FREECAD ASSEMBLY — COMPONENT RECIPES ("enclosure-assy")

This assembly document has 8 components, labeled P0..P7 below (a component is one placed body or linked part). 8 of them carry a construction recipe — the FreeCAD feature program that regenerates the part from scratch, quoted from this document or its linked companion documents; the rest are supplied as boundary geometry only. No exploded tour is included for this assembly.
COMPONENT P0 — recipe-attached ("exhaust-fan", a linked part whose construction recipe lives in a companion FreeCAD document of the same project; that document's serialized recipe follows).
Construction recipe (the companion document, serialized — sketch geometry with constraints, then the solid features built on it; lengths are millimeters unless a unit is written):

FCSTD DOCUMENT  (FreeCAD 1.1R40971 (Git))
Label: exhaust-fan
License: All rights reserved
LicenseURL: http://en.wikipedia.org/wiki/All_rights_reserved
objects: Sketcher::SketchObject×3, PartDesign::Revolution×1, PartDesign::Pad×1, App::Point×1, Part::Feature×1, PartDesign::Body×1
note: 14 computed .brp shape members not serialized (recipe doc carries the construction recipe); baked Part::Feature solids carry a one-line shape summary decoded from their .brp

FEATURE [Sketcher::SketchObject] Sketch
  ArcFitTolerance = 0
  AttachmentSupport = -> [XZ_Plane]
  ExternalTypes = [0]
  FullyConstrained = true
  MakeInternals = false
  MapMode = 5
  Placement = pos=(0,0,0) rot=(1,0,0;1.5708rad)
  expr: Constraints[35] = 3.67 in + 0.25 in
  sketch-geometry (22):
    g0: LineSegment StartX=-103.94 StartY=78.7817 StartZ=0 EndX=-62.5 EndY=93.2648 EndZ=0
    g1: LineSegment StartX=-62.5 StartY=93.2648 StartZ=0 EndX=-62.5 EndY=99.568 EndZ=0
    g2: LineSegment StartX=-62.5 StartY=99.568 StartZ=0 EndX=-52.5 EndY=99.568 EndZ=0
    g3: LineSegment StartX=-52.5 StartY=99.568 StartZ=0 EndX=-52.5 EndY=93.2648 EndZ=0
    g4: LineSegment StartX=-52.5 StartY=93.2648 StartZ=0 EndX=52.5 EndY=93.2648 EndZ=0
    g5: LineSegment StartX=52.5 StartY=93.2648 StartZ=0 EndX=52.5 EndY=99.568 EndZ=0
    g6: LineSegment StartX=52.5 StartY=99.568 StartZ=0 EndX=62.5 EndY=99.568 EndZ=0
    g7: LineSegment StartX=62.5 StartY=99.568 StartZ=0 EndX=62.5 EndY=93.2648 EndZ=0
    g8: LineSegment StartX=62.5 StartY=93.2648 StartZ=0 EndX=103.94 EndY=78.7817 EndZ=0
    g9: LineSegment StartX=-103.94 StartY=78.7817 StartZ=0 EndX=-116.94 EndY=78.7817 EndZ=0
    g10: LineSegment StartX=-116.94 StartY=78.7817 StartZ=0 EndX=-122.94 EndY=74.676 EndZ=0
    g11: LineSegment StartX=-122.94 StartY=74.676 StartZ=0 EndX=-154.94 EndY=74.676 EndZ=0
    g12: LineSegment StartX=103.94 StartY=78.7817 StartZ=0 EndX=116.94 EndY=78.7817 EndZ=0
    g13: LineSegment StartX=116.94 StartY=78.7817 StartZ=0 EndX=122.94 EndY=74.676 EndZ=0
    g14: LineSegment StartX=122.94 StartY=74.676 StartZ=0 EndX=154.94 EndY=74.676 EndZ=0
    g15: LineSegment StartX=-154.94 StartY=74.676 StartZ=0 EndX=-154.94 EndY=72.176 EndZ=0
    g16: LineSegment StartX=-154.94 StartY=72.176 StartZ=0 EndX=-54.94 EndY=72.176 EndZ=0
    g17: LineSegment StartX=-54.94 StartY=72.176 StartZ=0 EndX=-54.94 EndY=0 EndZ=0
    g18: LineSegment StartX=-54.94 StartY=0 StartZ=0 EndX=54.94 EndY=0 EndZ=0
    g19: LineSegment StartX=54.94 StartY=0 StartZ=0 EndX=54.94 EndY=72.176 EndZ=0
    g20: LineSegment StartX=54.94 StartY=72.176 StartZ=0 EndX=154.94 EndY=72.176 EndZ=0
    g21: LineSegment StartX=154.94 StartY=72.176 StartZ=0 EndX=154.94 EndY=74.676 EndZ=0
  constraints (62):
    c: Coincident(g0,g1)
    c: Coincident(g1,g2)
    c: Coincident(g2,g3)
    c: Coincident(g3,g4)
    c: Coincident(g4,g5)
    c: Coincident(g5,g6)
    c: Coincident(g6,g7)
    c: Coincident(g7,g8)
    c: Horizontal(g2)
    c: Horizontal(g6)
    c: Vertical(g3)
    c: Vertical(g1)
    c: Vertical(g5)
    c: Vertical(g7)
    c: PointOnObject(g0,g4)
    c: PointOnObject(g7,g4)
    c: Symmetric(g3,g4,g-2)
    c: Equal(g6,g2)
    c: DistanceY(g-1,g4) = 93.2648
    c: PointOnObject(g5,g2)
    c: DistanceX(g2,g2) = 10
    c: DistanceX(g4,g4) = 105
    c: Coincident(g0,g9)
    c: Coincident(g9,g10)
    c: Coincident(g10,g11)
    c: Coincident(g8,g12)
    c: Horizontal(g12)
    c: Coincident(g12,g13)
    c: Coincident(g13,g14)
    c: Horizontal(g14)
    c: Horizontal(g11)
    c: DistanceX(g11,g11) = 32
    c: Equal(g14,g11)
    c: DistanceX(g9,g9) = 13
    c: DistanceX(g11,g9) = 38
    c: DistanceY(g-1,g2) = 99.568
    c: Symmetric(g0,g8,g-2)
    c: Symmetric(g9,g12,g-2)
    c: Coincident(g11,g15)
    c: Coincident(g15,g16)
    c: Horizontal(g16)
    c: Coincident(g16,g17)
    c: DistanceY(g-1,g11) = 74.676
    c: Vertical(g17)
    c: DistanceX(g16,g16) = 100
    c: Vertical(g15)
    c: DistanceX(g11,g14) = 309.88
    c: Coincident(g17,g18)
    c: PointOnObject(g18,g-1)
    c: Horizontal(g18)
    c: Coincident(g18,g19)
    c: Vertical(g19)
    c: Coincident(g19,g20)
    c: Horizontal(g20)
    c: Coincident(g20,g21)
    c: Coincident(g21,g14)
    c: Equal(g21,g15)
    c: Vertical(g21)
    c: DistanceY(g21,g21) = 2.5
    c: Equal(g20,g16)
    c: Symmetric(g15,g20,g-2)
    c: DistanceY(g-1,g9) = 78.7817
FEATURE [PartDesign::Revolution] Revolution
  Angle = 360
  Angle2 = 60
  Axis = (1,0,0)
  Base = (0,0,0)
  Placement = pos=(0,0,0) rot=(1,0,0;1.5708rad)
  Profile = -> Sketch
  ReferenceAxis = -> Sketch [H_Axis]
  Suppressed = false
  Type = 0
FEATURE [Sketcher::SketchObject] Sketch001
  ArcFitTolerance = 0
  ExternalTypes = [0]
  FullyConstrained = true
  MakeInternals = false
  MapMode = 5
  Placement = pos=(0,0,76.2) rot=(0,0,1;0rad)
  sketch-geometry (12):
    g0: LineSegment StartX=-50.3 StartY=-59.944 StartZ=0 EndX=50.3 EndY=-59.944 EndZ=0
    g1: LineSegment StartX=63 StartY=-47.244 StartZ=0 EndX=63 EndY=47.244 EndZ=0
    g2: LineSegment StartX=50.3 StartY=59.944 StartZ=0 EndX=-50.3 EndY=59.944 EndZ=0
    g3: LineSegment StartX=-63 StartY=47.244 StartZ=0 EndX=-63 EndY=-47.244 EndZ=0
    g4: ArcOfCircle CenterX=-50.3 CenterY=47.244 CenterZ=0 NormalX=0 NormalY=0 NormalZ=1 AngleXU=0 Radius=12.7 StartAngle=1.5708 EndAngle=3.14159
    g5: GeomPoint [constr] X=-63 Y=59.944 Z=0
    g6: ArcOfCircle CenterX=50.3 CenterY=47.244 CenterZ=0 NormalX=0 NormalY=0 NormalZ=1 AngleXU=0 Radius=12.7 StartAngle=-6.39e-14 EndAngle=1.5708
    g7: GeomPoint [constr] X=63 Y=59.944 Z=0
    g8: ArcOfCircle CenterX=-50.3 CenterY=-47.244 CenterZ=0 NormalX=0 NormalY=0 NormalZ=1 AngleXU=0 Radius=12.7 StartAngle=3.14159 EndAngle=4.71239
    g9: GeomPoint [constr] X=-63 Y=-59.944 Z=0
    g10: ArcOfCircle CenterX=50.3 CenterY=-47.244 CenterZ=0 NormalX=0 NormalY=0 NormalZ=1 AngleXU=0 Radius=12.7 StartAngle=4.71239 EndAngle=6.28319
    g11: GeomPoint [constr] X=63 Y=-59.944 Z=0
  constraints (26):
    c: Horizontal(g0)
    c: Vertical(g1)
    c: Vertical(g3)
    c: DistanceX(g5,g7) = 126
    c: DistanceY(g11,g7) = 119.888
    c: Symmetric(g5,g7,g-2)
    c: PointOnObject(g5,g2)
    c: PointOnObject(g5,g3)
    c: Tangent(g2,g4) = -1.5708
    c: Tangent(g3,g4) = -1.5708
    c: PointOnObject(g7,g2)
    c: PointOnObject(g7,g1)
    c: Tangent(g2,g6) = -1.5708
    c: Tangent(g1,g6) = -1.5708
    c: PointOnObject(g9,g0)
    c: PointOnObject(g9,g3)
    c: Tangent(g0,g8) = -1.5708
    c: Tangent(g3,g8) = -1.5708
    c: PointOnObject(g11,g0)
    c: PointOnObject(g11,g1)
    c: Tangent(g0,g10) = -1.5708
    c: Tangent(g1,g10) = -1.5708
    c: Equal(g6,g4)
    c: Equal(g4,g8)
    c: Radius(g6) = 12.7
    c: Symmetric(g2,g0,g-1)
FEATURE [PartDesign::Pad] Pad
  BaseFeature = -> Revolution
  Direction = (0,0,1)
  Length = 41.402
  Length2 = 10
  Placement = pos=(0,0,0) rot=(1,0,0;1.5708rad)
  Profile = -> Sketch001
  ReferenceAxis = -> Sketch001 [N_Axis]
  Suppressed = false
  Type = 0
FEATURE [App::Point] Origin001  label="Origin"
  Role = Origin
FEATURE [Part::Feature] Body_cs
  shape: bbox 309.9 x 0.0004313 x 217.2 mm, 0 faces, 0 solids (baked)
FEATURE [Sketcher::SketchObject] Sketch002
  ArcFitTolerance = 1e-06
  AttachmentSupport = -> [XZ_Plane]
  ExternalTypes = [0]
  FullyConstrained = false
  MakeInternals = false
  MapMode = 5
  Placement = pos=(0,0,0) rot=(1,0,0;1.5708rad)
  sketch-geometry (1):
    g0: LineSegment StartX=-63 StartY=117.602 StartZ=0 EndX=63 EndY=117.602 EndZ=0
  constraints (2):
    c: Horizontal(g0)
    c: DistanceY(g-1,g0) = 117.602
FEATURE [PartDesign::Body] Body
  AllowCompound = false
  Group = -> [Sketch,Revolution,Sketch001,Pad,Sketch002]
  Origin = -> Origin
  Tip = -> Pad
COMPONENT P1 — recipe-attached ("gate", a linked part whose construction recipe lives in a companion FreeCAD document of the same project; that document's serialized recipe follows).
Construction recipe (the companion document, serialized — sketch geometry with constraints, then the solid features built on it; lengths are millimeters unless a unit is written):

FCSTD DOCUMENT  (FreeCAD 1.1R40971 (Git))
Label: blastgate
License: All rights reserved
LicenseURL: http://en.wikipedia.org/wiki/All_rights_reserved
objects: Sketcher::SketchObject×7, PartDesign::Pad×4, PartDesign::Pocket×3, PartDesign::Body×1, App::Point×1
note: 36 computed .brp shape members not serialized (recipe doc carries the construction recipe); baked Part::Feature solids carry a one-line shape summary decoded from their .brp

FEATURE [Sketcher::SketchObject] Sketch  label="sbody"
  ArcFitTolerance = 0
  AttachmentSupport = -> [XZ_Plane]
  ExternalTypes = [0]
  FullyConstrained = true
  MakeInternals = false
  MapMode = 5
  Placement = pos=(0,0,0) rot=(1,0,0;1.5708rad)
  sketch-geometry (27):
    g0: LineSegment StartX=-68.2548 StartY=133.177 StartZ=0 EndX=-61.5 EndY=102.9 EndZ=0
    g1: LineSegment StartX=-61.5 StartY=102.9 StartZ=0 EndX=61.5 EndY=102.9 EndZ=0
    g2: LineSegment StartX=61.5 StartY=102.9 StartZ=0 EndX=68.2548 EndY=133.177 EndZ=0
    g3: LineSegment StartX=78.0149 StartY=141 StartZ=0 EndX=80.9974 EndY=141 EndZ=0
    g4: LineSegment StartX=90.4563 StartY=127.755 StartZ=0 EndX=80.2487 EndY=98 EndZ=0
    g5: LineSegment StartX=80.2487 StartY=98 StartZ=0 EndX=80.2487 EndY=55 EndZ=0
    g6: LineSegment StartX=80.2487 StartY=-82 StartZ=0 EndX=-79.7513 EndY=-82 EndZ=0
    g7: LineSegment StartX=-79.7513 StartY=-62 StartZ=0 EndX=-79.7513 EndY=35 EndZ=0
    g8: LineSegment StartX=-79.7513 StartY=96.55 StartZ=0 EndX=-90.4563 EndY=127.755 EndZ=0
    g9: LineSegment StartX=-80.9974 StartY=141 StartZ=0 EndX=-78.0149 EndY=141 EndZ=0
    g10: Circle [constr] CenterX=0 CenterY=0 CenterZ=0 NormalX=0 NormalY=0 NormalZ=1 AngleXU=0 Radius=71
    g11: GeomPoint [constr] X=0 Y=-71 Z=0
    g12: ArcOfCircle CenterX=-79.7513 CenterY=-72 CenterZ=0 NormalX=0 NormalY=0 NormalZ=1 AngleXU=0 Radius=10 StartAngle=1.5708 EndAngle=4.71239
    g13: ArcOfCircle CenterX=80.2487 CenterY=-72 CenterZ=0 NormalX=0 NormalY=0 NormalZ=1 AngleXU=0 Radius=10 StartAngle=4.71239 EndAngle=7.85398
    g14: ArcOfCircle CenterX=-79.7513 CenterY=45 CenterZ=0 NormalX=0 NormalY=0 NormalZ=1 AngleXU=0 Radius=10 StartAngle=1.5708 EndAngle=4.71239
    g15: ArcOfCircle CenterX=80.2487 CenterY=45 CenterZ=0 NormalX=0 NormalY=0 NormalZ=1 AngleXU=0 Radius=10 StartAngle=4.71239 EndAngle=7.85398
    g16: LineSegment StartX=80.2487 StartY=35 StartZ=0 EndX=80.2487 EndY=-62 EndZ=0
    g17: LineSegment StartX=-79.7513 StartY=55 StartZ=0 EndX=-79.7513 EndY=96.55 EndZ=0
    g18: ArcOfCircle CenterX=-80.9974 CenterY=131 CenterZ=0 NormalX=0 NormalY=0 NormalZ=1 AngleXU=0 Radius=10 StartAngle=1.5708 EndAngle=3.47206
    g19: GeomPoint [constr] X=-95 Y=141 Z=0
    g20: ArcOfCircle CenterX=80.9974 CenterY=131 CenterZ=0 NormalX=0 NormalY=0 NormalZ=1 AngleXU=0 Radius=10 StartAngle=5.95271 EndAngle=7.85398
    g21: GeomPoint [constr] X=95 Y=141 Z=0
    g22: ArcOfCircle CenterX=-78.0149 CenterY=131 CenterZ=0 NormalX=0 NormalY=0 NormalZ=1 AngleXU=0 Radius=10 StartAngle=0.219503 EndAngle=1.5708
    g23: GeomPoint [constr] X=-70 Y=141 Z=0
    g24: ArcOfCircle CenterX=78.0149 CenterY=131 CenterZ=0 NormalX=0 NormalY=0 NormalZ=1 AngleXU=0 Radius=10 StartAngle=1.5708 EndAngle=2.92209
    g25: GeomPoint [constr] X=70 Y=141 Z=0
    g26: Circle [constr] CenterX=0 CenterY=0 CenterZ=0 NormalX=0 NormalY=0 NormalZ=1 AngleXU=0 Radius=74.6125
  constraints (69):
    c: Coincident(g0,g1)
    c: Coincident(g1,g2)
    c: Horizontal(g3)
    c: Coincident(g4,g5)
    c: Vertical(g5)
    c: Vertical(g7)
    c: Coincident(g17,g8)
    c: Diameter(g10) = 142
    c: Coincident(g10,g-1)
    c: DistanceX(g6,g6) = 160
    c: DistanceY(g6,g23) = 223
    c: Horizontal(g9)
    c: DistanceX(g23,g25) = 140
    c: Symmetric(g25,g23,g-2)
    c: DistanceY(g0,g23) = 38.1
    c: DistanceX(g19,g21) = 190
    c: PointOnObject(g11,g10)
    c: PointOnObject(g11,g-2)
    c: DistanceY(g6,g11) = 11
    c: DistanceY(g6,g4) = 180
    c: Symmetric(g1,g0,g-2)
    c: Diameter(g12) = 20
    c: Equal(g13,g12)
    c: PointOnObject(g14,g7)
    c: PointOnObject(g15,g5)
    c: Equal(g12,g14)
    c: Equal(g14,g15)
    c: DistanceY(g12,g14) = 117
    c: Tangent(g12,g6) = 1.5708
    c: Coincident(g7,g12)
    c: Tangent(g13,g6) = 1.5708
    c: Coincident(g16,g13)
    c: Coincident(g5,g15)
    c: Coincident(g16,g15)
    c: Coincident(g14,g7)
    c: Coincident(g14,g17)
    c: Horizontal(g15,g14)
    c: PointOnObject(g19,g8)
    c: PointOnObject(g19,g9)
    c: Tangent(g8,g18) = 1.5708
    c: Tangent(g9,g18) = 1.5708
    c: PointOnObject(g21,g4)
    c: PointOnObject(g21,g3)
    c: Tangent(g4,g20) = 1.5708
    c: Tangent(g3,g20) = 1.5708
    c: Equal(g20,g18)
    c: Radius(g20) = 10
    c: DistanceX(g1,g1) = 123
    c: PointOnObject(g23,g9)
    c: PointOnObject(g23,g0)
    c: Tangent(g9,g22) = 1.5708
    c: Tangent(g0,g22) = 1.5708
    c: PointOnObject(g25,g3)
    c: PointOnObject(g25,g2)
    c: Tangent(g3,g24) = 1.5708
    c: Tangent(g2,g24) = 1.5708
    c: Equal(g24,g20)
    c: Equal(g20,g22)
    c: DistanceY(g8,g9) = 44.45
    c: Symmetric(g8,g4,g-2)
    c: Horizontal(g6)
    c: Perpendicular(g13,g16)
    c: Perpendicular(g12,g7)
    c: Vertical(g17)
    c: PointOnObject(g14,g7)
    c: PointOnObject(g5,g16)
    c: Equal(g7,g16)
    c: Coincident(g26,g10)
    c: Diameter(g26) = 149.225
FEATURE [PartDesign::Pad] Pad
  Direction = (0,-1,2e-16)
  Length = 12.7
  Length2 = 10
  Midplane = true
  Placement = pos=(0,0,0) rot=(1,0,0;1.5708rad)
  Profile = -> Sketch
  ReferenceAxis = -> Sketch [N_Axis]
  Suppressed = false
  Type = 0
FEATURE [Sketcher::SketchObject] Sketch001  label="scollar"
  ArcFitTolerance = 0
  ExternalTypes = [0]
  FullyConstrained = true
  MakeInternals = false
  MapMode = 5
  Placement = pos=(0,0,0) rot=(1,0,0;1.5708rad)
  expr: Constraints[2] = 5.88 in
  sketch-geometry (2):
    g0: Circle [constr] CenterX=0 CenterY=0 CenterZ=0 NormalX=0 NormalY=0 NormalZ=1 AngleXU=0 Radius=71.4375
    g1: Circle CenterX=0 CenterY=0 CenterZ=0 NormalX=0 NormalY=0 NormalZ=1 AngleXU=0 Radius=74.676
  constraints (4):
    c: Coincident(g0,g-1)
    c: Coincident(g1,g0)
    c: Diameter(g1) = 149.352
    c: Diameter(g0) = 142.875
FEATURE [PartDesign::Pad] Pad001
  BaseFeature = -> Pad
  Direction = (0,-1,2e-16)
  Length = 89.916
  Length2 = 10
  Midplane = true
  Placement = pos=(0,0,0) rot=(1,0,0;1.5708rad)
  Profile = -> Sketch001
  ReferenceAxis = -> Sketch001 [N_Axis]
  Suppressed = false
  Type = 0
FEATURE [Sketcher::SketchObject] Sketch002  label="sboss"
  ArcFitTolerance = 0
  ExternalTypes = [0]
  FullyConstrained = true
  MakeInternals = false
  MapMode = 3
  Placement = pos=(0,0,0) rot=(1,0,0;1.5708rad)
  sketch-geometry (2):
    g0: Circle CenterX=0 CenterY=96.52 CenterZ=0 NormalX=0 NormalY=0 NormalZ=1 AngleXU=0 Radius=6
    g1: Circle [constr] CenterX=0 CenterY=96.52 CenterZ=0 NormalX=0 NormalY=0 NormalZ=1 AngleXU=0 Radius=2.5
  constraints (5):
    c: PointOnObject(g0,g-2)
    c: Diameter(g0) = 12
    c: Coincident(g1,g0)
    c: Diameter(g1) = 5
    c: DistanceY(g-1,g0) = 96.52
FEATURE [Sketcher::SketchObject] s_date  label="sgate"
  ArcFitTolerance = 0
  ExternalTypes = [0]
  FullyConstrained = true
  MakeInternals = false
  Placement = pos=(0,0,0) rot=(1,0,0;1.5708rad)
  sketch-geometry (8):
    g0: LineSegment StartX=-52.3875 StartY=254 StartZ=0 EndX=52.3875 EndY=254 EndZ=0
    g1: LineSegment StartX=-52.3875 StartY=254 StartZ=0 EndX=-73.025 EndY=232.664 EndZ=0
    g2: LineSegment StartX=52.3875 StartY=254 StartZ=0 EndX=73.025 EndY=232.664 EndZ=0
    g3: LineSegment StartX=-73.025 StartY=232.664 StartZ=0 EndX=-98.425 EndY=232.664 EndZ=0
    g4: LineSegment StartX=-98.425 StartY=232.664 StartZ=0 EndX=-98.425 EndY=283.464 EndZ=0
    g5: LineSegment StartX=-98.425 StartY=283.464 StartZ=0 EndX=98.425 EndY=283.464 EndZ=0
    g6: LineSegment StartX=98.425 StartY=283.464 StartZ=0 EndX=98.425 EndY=232.664 EndZ=0
    g7: LineSegment StartX=98.425 StartY=232.664 StartZ=0 EndX=73.025 EndY=232.664 EndZ=0
  constraints (23):
    c: Coincident(g0,g1)
    c: Coincident(g0,g2)
    c: DistanceY(g-1,g0) = 254
    c: DistanceX(g1,g2) = 146.05
    c: Equal(g2,g1)
    c: Symmetric(g2,g1,g-2)
    c: Horizontal(g0)
    c: DistanceX(g0,g0) = 104.775
    c: Coincident(g1,g3)
    c: Horizontal(g3)
    c: Coincident(g3,g4)
    c: Vertical(g4)
    c: Coincident(g4,g5)
    c: Coincident(g5,g6)
    c: Coincident(g6,g7)
    c: Coincident(g7,g2)
    c: Horizontal(g7)
    c: Horizontal(g5)
    c: Vertical(g6)
    c: Equal(g3,g7)
    c: DistanceX(g7,g7) = 25.4
    c: DistanceY(g-1,g2) = 232.664
    c: DistanceY(g6,g6) = 50.8
FEATURE [Sketcher::SketchObject] Sketch003  label="sthru"
  ArcFitTolerance = 0
  ExternalTypes = [0]
  FullyConstrained = true
  MakeInternals = false
  MapMode = 5
  Placement = pos=(0,0,0) rot=(1,0,0;1.5708rad)
  expr: Constraints[2] = 5.88 in
  sketch-geometry (2):
    g0: Circle CenterX=0 CenterY=0 CenterZ=0 NormalX=0 NormalY=0 NormalZ=1 AngleXU=0 Radius=71.4375
    g1: Circle [constr] CenterX=0 CenterY=0 CenterZ=0 NormalX=0 NormalY=0 NormalZ=1 AngleXU=0 Radius=74.676
  constraints (4):
    c: Coincident(g0,g-1)
    c: Coincident(g1,g0)
    c: Diameter(g1) = 149.352
    c: Diameter(g0) = 142.875
FEATURE [PartDesign::Pocket] Pocket
  BaseFeature = -> Pad001
  Direction = (0,1,0)
  Length = 5
  Length2 = 5
  Midplane = true
  Placement = pos=(0,0,0) rot=(1,0,0;1.5708rad)
  Profile = -> Sketch003
  ReferenceAxis = -> Sketch003 [N_Axis]
  Suppressed = false
  Type = 1
  UseCustomVector = true
FEATURE [Sketcher::SketchObject] Sketch004  label="sstop"
  ArcFitTolerance = 0
  ExternalTypes = [0]
  FullyConstrained = true
  MakeInternals = false
  MapMode = 3
  Placement = pos=(0,0,0) rot=(1,0,0;1.5708rad)
  sketch-geometry (2):
    g0: Circle [constr] CenterX=0 CenterY=96.52 CenterZ=0 NormalX=0 NormalY=0 NormalZ=1 AngleXU=0 Radius=6
    g1: Circle CenterX=0 CenterY=96.52 CenterZ=0 NormalX=0 NormalY=0 NormalZ=1 AngleXU=0 Radius=2.5
  constraints (5):
    c: PointOnObject(g0,g-2)
    c: Diameter(g0) = 12
    c: Coincident(g1,g0)
    c: Diameter(g1) = 5
    c: DistanceY(g-1,g0) = 96.52
FEATURE [PartDesign::Pad] Pad002
  BaseFeature = -> Pocket
  Direction = (0,-1,2e-16)
  Length = 21
  Length2 = 10
  Midplane = true
  Placement = pos=(0,0,0) rot=(1,0,0;1.5708rad)
  Profile = -> Sketch002
  ReferenceAxis = -> Sketch002 [N_Axis]
  Suppressed = false
  Type = 0
FEATURE [PartDesign::Pocket] Pocket001
  BaseFeature = -> Pad002
  Direction = (0,1,-2e-16)
  Length = 5
  Length2 = 5
  Midplane = true
  Placement = pos=(0,0,0) rot=(1,0,0;1.5708rad)
  Profile = -> Sketch004
  ReferenceAxis = -> Sketch004 [N_Axis]
  Suppressed = false
  Type = 1
FEATURE [Sketcher::SketchObject] Sketch005
  ArcFitTolerance = 0
  AttachmentSupport = -> [s_date]
  ExternalTypes = [0]
  FullyConstrained = false
  MakeInternals = false
  MapMode = 4
  Placement = pos=(0,0,0) rot=(0.707107,0,0.707107;3.14159rad)
  sketch-geometry (6):
    g0: LineSegment StartX=76.2 StartY=0.603403 StartZ=0 EndX=254 EndY=0.603403 EndZ=0
    g1: LineSegment StartX=254 StartY=0.603403 StartZ=0 EndX=254 EndY=-12.0966 EndZ=0
    g2: LineSegment StartX=254 StartY=-12.0966 StartZ=0 EndX=253 EndY=-12.0966 EndZ=0
    g3: LineSegment StartX=253 StartY=-12.0966 StartZ=0 EndX=253 EndY=-0.396597 EndZ=0
    g4: LineSegment StartX=253 StartY=-0.396597 StartZ=0 EndX=76.2 EndY=-0.396597 EndZ=0
    g5: LineSegment StartX=76.2 StartY=-0.396597 StartZ=0 EndX=76.2 EndY=0.603403 EndZ=0
  constraints (17):
    c: Horizontal(g0)
    c: Coincident(g0,g1)
    c: Coincident(g1,g2)
    c: Coincident(g2,g3)
    c: Coincident(g3,g4)
    c: Horizontal(g4)
    c: Coincident(g4,g5)
    c: Coincident(g5,g0)
    c: Vertical(g5)
    c: Vertical(g3)
    c: Vertical(g1)
    c: Horizontal(g2)
    c: DistanceX(g2,g2) = 1
    c: DistanceX(g-1,g0) = 254
    c: DistanceY(g1,g1) = 12.7
    c: Equal(g5,g2)
    c: DistanceX(g-1,g0) = 76.2
FEATURE [PartDesign::Pad] Pad003
  BaseFeature = -> Pocket001
  Direction = (1,0,-2e-16)
  Length = 146.05
  Length2 = 10
  Midplane = true
  Placement = pos=(0,0,0) rot=(1,0,0;1.5708rad)
  Profile = -> Sketch005
  ReferenceAxis = -> Sketch005 [N_Axis]
  Suppressed = false
  Type = 0
FEATURE [PartDesign::Pocket] Pocket002
  BaseFeature = -> Pad003
  Direction = (0,1,-2e-16)
  Length = 5
  Length2 = 5
  Midplane = true
  Placement = pos=(0,0,0) rot=(1,0,0;1.5708rad)
  Profile = -> s_date
  ReferenceAxis = -> s_date [N_Axis]
  Suppressed = false
  Type = 1
FEATURE [PartDesign::Body] Body
  AllowCompound = false
  Group = -> [Sketch,Pad,Sketch001,Pad001,Sketch002,s_date,Sketch003,Pocket,Sketch004,Pad002,Pocket001,Sketch005,Pad003,Pocket002]
  Origin = -> Origin
  Tip = -> Pocket002
FEATURE [App::Point] Origin001  label="Origin"
  Role = Origin
COMPONENT P2 — recipe-attached ("square-to-round", a linked part whose construction recipe lives in a companion FreeCAD document of the same project; that document's serialized recipe follows).
Construction recipe (the companion document, serialized — sketch geometry with constraints, then the solid features built on it; lengths are millimeters unless a unit is written):

FCSTD DOCUMENT  (FreeCAD 1.1R40971 (Git))
Label: square-to-round
License: All rights reserved
LicenseURL: http://en.wikipedia.org/wiki/All_rights_reserved
objects: Sketcher::SketchObject×7, PartDesign::Body×3, App::Point×3, PartDesign::Pad×1, PartDesign::AdditiveLoft×1
note: 23 computed .brp shape members not serialized (recipe doc carries the construction recipe); baked Part::Feature solids carry a one-line shape summary decoded from their .brp

FEATURE [Sketcher::SketchObject] Sketch  label="square"
  ArcFitTolerance = 1e-06
  ExternalTypes = [0]
  FullyConstrained = true
  MakeInternals = false
  MapMode = 4
  Placement = pos=(0,0,0) rot=(0.57735,0.57735,0.57735;2.0944rad)
  sketch-geometry (8):
    g0: LineSegment StartX=-152.4 StartY=136.398 StartZ=0 EndX=-152.4 EndY=-117.602 EndZ=0
    g1: LineSegment StartX=-152.4 StartY=-117.602 StartZ=0 EndX=152.4 EndY=-117.602 EndZ=0
    g2: LineSegment StartX=152.4 StartY=-117.602 StartZ=0 EndX=152.4 EndY=136.398 EndZ=0
    g3: LineSegment StartX=152.4 StartY=136.398 StartZ=0 EndX=-152.4 EndY=136.398 EndZ=0
    g4: LineSegment StartX=-149.225 StartY=133.223 StartZ=0 EndX=-149.225 EndY=-114.3 EndZ=0
    g5: LineSegment StartX=-149.225 StartY=-114.3 StartZ=0 EndX=149.225 EndY=-114.3 EndZ=0
    g6: LineSegment StartX=149.225 StartY=-114.3 StartZ=0 EndX=149.225 EndY=133.223 EndZ=0
    g7: LineSegment StartX=149.225 StartY=133.223 StartZ=0 EndX=-149.225 EndY=133.223 EndZ=0
  constraints (22):
    c: Coincident(g0,g1)
    c: Coincident(g1,g2)
    c: Vertical(g0)
    c: Coincident(g4,g5)
    c: Coincident(g5,g6)
    c: Coincident(g6,g7)
    c: Coincident(g7,g4)
    c: Vertical(g4)
    c: DistanceY(g2,g2) = 254
    c: DistanceX(g5,g1) = 3.175
    c: DistanceY(g6,g2) = 3.175
    c: DistanceY(g1,g5) = 3.302
    c: Vertical(g6)
    c: Vertical(g2)
    c: Coincident(g0,g3)
    c: Coincident(g2,g3)
    c: Symmetric(g2,g0,g-2)
    c: Symmetric(g4,g6,g-2)
    c: Horizontal(g1)
    c: Horizontal(g5)
    c: DistanceY(g1,g-1) = 117.602
    c: DistanceX(g3,g3) = 304.8
FEATURE [Sketcher::SketchObject] Sketch002  label="path"
  ArcFitTolerance = 1e-06
  ExternalTypes = [0]
  FullyConstrained = true
  MakeInternals = false
  MapMode = 4
  Placement = pos=(0,0,0) rot=(1,0,0;1.5708rad)
  sketch-geometry (1):
    g0: LineSegment StartX=0 StartY=0 StartZ=0 EndX=279.4 EndY=-9.398 EndZ=0
  constraints (3):
    c: Coincident(g0,g-1)
    c: DistanceX(g0,g0) = 279.4
    c: DistanceY(g0,g-1) = 9.398
FEATURE [Sketcher::SketchObject] Sketch001  label="round"
  ArcFitTolerance = 1e-06
  AttachmentSupport = -> [Sketch002]
  ExternalTypes = [0]
  FullyConstrained = true
  MakeInternals = false
  MapMode = 1
  Placement = pos=(279.4,2.1e-15,-9.398) rot=(0.57735,0.57735,0.57735;2.0944rad)
  sketch-geometry (34):
    g0: LineSegment StartX=0 StartY=76.2 StartZ=0 EndX=-29.1605 EndY=70.3996 EndZ=0
    g1: LineSegment StartX=-29.1605 StartY=70.3996 StartZ=0 EndX=-53.8815 EndY=53.8815 EndZ=0
    g2: LineSegment StartX=-53.8815 StartY=53.8815 StartZ=0 EndX=-70.3996 EndY=29.1605 EndZ=0
    g3: LineSegment StartX=-70.3996 StartY=29.1605 StartZ=0 EndX=-76.2 EndY=-3.6e-15 EndZ=0
    g4: LineSegment StartX=-76.2 StartY=-3.6e-15 StartZ=0 EndX=-70.3996 EndY=-29.1605 EndZ=0
    g5: LineSegment StartX=-70.3996 StartY=-29.1605 StartZ=0 EndX=-53.8815 EndY=-53.8815 EndZ=0
    g6: LineSegment StartX=-53.8815 StartY=-53.8815 StartZ=0 EndX=-29.1605 EndY=-70.3996 EndZ=0
    g7: LineSegment StartX=-29.1605 StartY=-70.3996 StartZ=0 EndX=3.6e-15 EndY=-76.2 EndZ=0
    g8: LineSegment StartX=3.6e-15 StartY=-76.2 StartZ=0 EndX=29.1605 EndY=-70.3996 EndZ=0
    g9: LineSegment StartX=29.1605 StartY=-70.3996 StartZ=0 EndX=53.8815 EndY=-53.8815 EndZ=0
    g10: LineSegment StartX=53.8815 StartY=-53.8815 StartZ=0 EndX=70.3996 EndY=-29.1605 EndZ=0
    g11: LineSegment StartX=70.3996 StartY=-29.1605 StartZ=0 EndX=76.2 EndY=0 EndZ=0
    g12: LineSegment StartX=76.2 StartY=0 StartZ=0 EndX=70.3996 EndY=29.1605 EndZ=0
    g13: LineSegment StartX=70.3996 StartY=29.1605 StartZ=0 EndX=53.8815 EndY=53.8815 EndZ=0
    g14: LineSegment StartX=53.8815 StartY=53.8815 StartZ=0 EndX=29.1605 EndY=70.3996 EndZ=0
    g15: LineSegment StartX=29.1605 StartY=70.3996 StartZ=0 EndX=0 EndY=76.2 EndZ=0
    g16: Circle [constr] CenterX=0 CenterY=0 CenterZ=0 NormalX=0 NormalY=0 NormalZ=1 AngleXU=0 Radius=76.2
    g17: LineSegment StartX=30.3755 StartY=73.3329 StartZ=0 EndX=0 EndY=79.375 EndZ=0
    g18: LineSegment StartX=0 StartY=79.375 StartZ=0 EndX=-30.3755 EndY=73.3329 EndZ=0
    g19: LineSegment StartX=-30.3755 StartY=73.3329 StartZ=0 EndX=-56.1266 EndY=56.1266 EndZ=0
    g20: LineSegment StartX=-56.1266 StartY=56.1266 StartZ=0 EndX=-73.3329 EndY=30.3755 EndZ=0
    g21: LineSegment StartX=-73.3329 StartY=30.3755 StartZ=0 EndX=-79.375 EndY=-3.6e-15 EndZ=0
    g22: LineSegment StartX=-79.375 StartY=-3.6e-15 StartZ=0 EndX=-73.3329 EndY=-30.3755 EndZ=0
    g23: LineSegment StartX=-73.3329 StartY=-30.3755 StartZ=0 EndX=-56.1266 EndY=-56.1266 EndZ=0
    g24: LineSegment StartX=-56.1266 StartY=-56.1266 StartZ=0 EndX=-30.3755 EndY=-73.3329 EndZ=0
    g25: LineSegment StartX=-30.3755 StartY=-73.3329 StartZ=0 EndX=-3.6e-15 EndY=-79.375 EndZ=0
    g26: LineSegment StartX=-3.6e-15 StartY=-79.375 StartZ=0 EndX=30.3755 EndY=-73.3329 EndZ=0
    g27: LineSegment StartX=30.3755 StartY=-73.3329 StartZ=0 EndX=56.1266 EndY=-56.1266 EndZ=0
    g28: LineSegment StartX=56.1266 StartY=-56.1266 StartZ=0 EndX=73.3329 EndY=-30.3755 EndZ=0
    g29: LineSegment StartX=73.3329 StartY=-30.3755 StartZ=0 EndX=79.375 EndY=3.6e-15 EndZ=0
    g30: LineSegment StartX=79.375 StartY=3.6e-15 StartZ=0 EndX=73.3329 EndY=30.3755 EndZ=0
    g31: LineSegment StartX=73.3329 StartY=30.3755 StartZ=0 EndX=56.1266 EndY=56.1266 EndZ=0
    g32: LineSegment StartX=56.1266 StartY=56.1266 StartZ=0 EndX=30.3755 EndY=73.3329 EndZ=0
    g33: Circle [constr] CenterX=0 CenterY=0 CenterZ=0 NormalX=0 NormalY=0 NormalZ=1 AngleXU=0 Radius=79.375
  constraints (72):
    c: Coincident(g0,g1)
    c: Coincident(g1,g2)
    c: Coincident(g2,g3)
    c: Coincident(g3,g4)
    c: Coincident(g4,g5)
    c: Coincident(g5,g6)
    c: Coincident(g6,g7)
    c: Coincident(g7,g8)
    c: Coincident(g8,g9)
    c: Coincident(g9,g10)
    c: Coincident(g10,g11)
    c: Coincident(g11,g12)
    c: Coincident(g12,g13)
    c: Coincident(g13,g14)
    c: Coincident(g14,g15)
    c: Coincident(g15,g0)
    c: Equal(g0, g1-g15) x15
    c: PointOnObject(g0,g16)
    c: PointOnObject(g1,g16)
    c: PointOnObject(g2,g16)
    c: PointOnObject(g3,g16)
    c: PointOnObject(g4,g16)
    c: PointOnObject(g5,g16)
    c: PointOnObject(g6,g16)
    c: PointOnObject(g7,g16)
    c: PointOnObject(g8,g16)
    c: PointOnObject(g9,g16)
    c: PointOnObject(g10,g16)
    c: PointOnObject(g11,g16)
    c: PointOnObject(g12,g16)
    c: PointOnObject(g13,g16)
    c: PointOnObject(g14,g16)
    c: PointOnObject(g15,g16)
    c: Vertical(g16,g0)
    c: Diameter(g16) = 152.4
    c: Coincident(g17,g18)
    c: Coincident(g18,g19)
    c: Coincident(g19,g20)
    c: Coincident(g20,g21)
    c: Coincident(g21,g22)
    c: Coincident(g22,g23)
    c: Coincident(g23,g24)
    c: Coincident(g24,g25)
    c: Coincident(g25,g26)
    c: Coincident(g26,g27)
    c: Coincident(g27,g28)
    c: Coincident(g28,g29)
    c: Coincident(g29,g30)
    c: Coincident(g30,g31)
    c: Coincident(g31,g32)
    c: Coincident(g32,g17)
    c: Equal(g17, g18-g32) x15
    c: PointOnObject(g17,g33)
    c: PointOnObject(g18,g33)
    c: PointOnObject(g19,g33)
    c: PointOnObject(g20,g33)
    c: PointOnObject(g21,g33)
    c: PointOnObject(g22,g33)
    c: PointOnObject(g23,g33)
    c: PointOnObject(g24,g33)
    c: PointOnObject(g25,g33)
    c: PointOnObject(g26,g33)
    c: PointOnObject(g27,g33)
    c: PointOnObject(g28,g33)
    c: PointOnObject(g29,g33)
    c: PointOnObject(g30,g33)
    c: PointOnObject(g31,g33)
    c: PointOnObject(g32,g33)
    c: Vertical(g33,g17)
    c: Diameter(g33) = 158.75
    c: Coincident(g16,g33)
    c: Coincident(g-1,g16)
FEATURE [Sketcher::SketchObject] Sketch003
  ArcFitTolerance = 1e-06
  AttachmentSupport = -> [XY_Plane001]
  ExternalTypes = [0]
  FullyConstrained = true
  MakeInternals = false
  MapMode = 5
  sketch-geometry (23):
    g0: LineSegment StartX=-285.284 StartY=67.6473 StartZ=0 EndX=-177.8 EndY=0 EndZ=0
    g1: LineSegment StartX=-177.8 StartY=0 StartZ=0 EndX=177.8 EndY=0 EndZ=0
    g2: LineSegment StartX=177.8 StartY=0 StartZ=0 EndX=285.284 EndY=67.6473 EndZ=0
    g3: LineSegment StartX=285.284 StartY=67.6473 StartZ=0 EndX=114.136 EndY=339.582 EndZ=0
    g4: LineSegment StartX=114.136 StartY=339.582 StartZ=0 EndX=87.7798 EndY=325.342 EndZ=0
    g5: LineSegment StartX=87.7798 StartY=325.342 StartZ=0 EndX=59.4511 EndY=315.597 EndZ=0
    g6: LineSegment StartX=59.4511 StartY=315.597 StartZ=0 EndX=29.9295 EndY=310.504 EndZ=0
    g7: LineSegment StartX=29.9295 StartY=310.504 StartZ=0 EndX=0 EndY=309.204 EndZ=0
    g8: LineSegment StartX=0 StartY=309.204 StartZ=0 EndX=-29.9295 EndY=310.504 EndZ=0
    g9: LineSegment StartX=-29.9295 StartY=310.504 StartZ=0 EndX=-59.4511 EndY=315.597 EndZ=0
    g10: LineSegment StartX=-59.4511 StartY=315.597 StartZ=0 EndX=-87.7798 EndY=325.342 EndZ=0
    g11: LineSegment StartX=-87.7798 StartY=325.342 StartZ=0 EndX=-114.136 EndY=339.582 EndZ=0
    g12: LineSegment StartX=-114.136 StartY=339.582 StartZ=0 EndX=-285.284 EndY=67.6473 EndZ=0
    g13: LineSegment [constr] StartX=0 StartY=309.204 StartZ=0 EndX=177.8 EndY=0 EndZ=0
    g14: LineSegment [constr] StartX=177.8 StartY=0 StartZ=0 EndX=29.9295 EndY=310.504 EndZ=0
    g15: LineSegment [constr] StartX=177.8 StartY=0 StartZ=0 EndX=114.136 EndY=339.582 EndZ=0
    g16: LineSegment [constr] StartX=-177.8 StartY=0 StartZ=0 EndX=-29.9295 EndY=310.504 EndZ=0
    g17: LineSegment [constr] StartX=-59.4511 StartY=315.597 StartZ=0 EndX=-177.8 EndY=0 EndZ=0
    g18: LineSegment [constr] StartX=-177.8 StartY=0 StartZ=0 EndX=-87.7798 EndY=325.342 EndZ=0
    g19: LineSegment [constr] StartX=-114.136 StartY=339.582 StartZ=0 EndX=-177.8 EndY=0 EndZ=0
    g20: LineSegment [constr] StartX=177.8 StartY=0 StartZ=0 EndX=59.4511 EndY=315.597 EndZ=0
    g21: LineSegment [constr] StartX=87.7798 StartY=325.342 StartZ=0 EndX=177.8 EndY=0 EndZ=0
    g22: LineSegment [constr] StartX=-177.8 StartY=0 StartZ=0 EndX=0 EndY=309.204 EndZ=0
  constraints (58):
    c: Coincident(g0,g1)
    c: Coincident(g1,g2)
    c: Coincident(g2,g3)
    c: Coincident(g3,g4)
    c: Coincident(g4,g5)
    c: Coincident(g5,g6)
    c: Coincident(g6,g7)
    c: Coincident(g7,g8)
    c: Coincident(g8,g9)
    c: Coincident(g9,g10)
    c: Coincident(g10,g11)
    c: Coincident(g11,g12)
    c: Coincident(g12,g0)
    c: PointOnObject(g7,g-2)
    c: Coincident(g13,g7)
    c: Coincident(g13,g1)
    c: Coincident(g14,g1)
    c: Coincident(g14,g6)
    c: Coincident(g15,g1)
    c: Coincident(g15,g3)
    c: Coincident(g16,g0)
    c: Coincident(g16,g8)
    c: Coincident(g17,g9)
    c: Coincident(g17,g0)
    c: Coincident(g18,g0)
    c: Coincident(g18,g10)
    c: Coincident(g19,g11)
    c: Coincident(g19,g0)
    c: Coincident(g20,g1)
    c: Coincident(g20,g5)
    c: Coincident(g21,g4)
    c: Coincident(g21,g1)
    c: Coincident(g22,g0)
    c: Coincident(g22,g7)
    c: Symmetric(g0,g1,g-2)
    c: PointOnObject(g0,g-1)
    c: DistanceX(g1,g1) = 355.6
    c: Distance(g2) = 127
    c: Distance(g3) = 321.31
    c: Equal(g4,g5)
    c: Equal(g5,g6)
    c: Equal(g6,g7)
    c: Equal(g7,g8)
    c: Equal(g8,g9)
    c: Equal(g9,g10)
    c: Equal(g10,g11)
    c: Equal(g12,g3)
    c: Equal(g0,g2)
    c: Perpendicular(g2,g3)
    c: Angle(g13,g1) = 1.04894
    c: Distance(g14) = 343.916
    c: Distance(g20) = 337.058
    c: Distance(g21) = 337.566
    c: Equal(g16,g14)
    c: Equal(g17,g20)
    c: Equal(g21,g18)
    c: Equal(g19,g15)
    c: Distance(g7,g3) = 118.11
FEATURE [PartDesign::Pad] Pad
  Direction = (0,0,1)
  Length = 3.175
  Length2 = 10
  Profile = -> Sketch003
  ReferenceAxis = -> Sketch003 [N_Axis]
  Suppressed = false
  Type = 0
FEATURE [PartDesign::Body] Body001  label="manufacturing"
  AllowCompound = false
  Group = -> [Sketch003,Pad]
  Origin = -> Origin001
  Tip = -> Pad
FEATURE [PartDesign::AdditiveLoft] AdditiveLoft
  Closed = true
  Placement = pos=(0,0,0) rot=(0.57735,0.57735,0.57735;2.0944rad)
  Profile = -> Sketch
  Ruled = true
  Sections = -> [Sketch001]
  Suppressed = false
FEATURE [PartDesign::Body] Body  label="Lofted"
  AllowCompound = false
  Group = -> [Sketch,Sketch001,Sketch002,AdditiveLoft]
  Origin = -> Origin
  Tip = -> AdditiveLoft
FEATURE [Sketcher::SketchObject] Sketch004  label="square001"
  ArcFitTolerance = 1e-06
  ExternalTypes = [0]
  FullyConstrained = true
  MakeInternals = false
  MapMode = 4
  Placement = pos=(0,0,0) rot=(0.57735,0.57735,0.57735;2.0944rad)
  sketch-geometry (4):
    g0: LineSegment StartX=-177.8 StartY=127 StartZ=0 EndX=-177.8 EndY=-127 EndZ=0
    g1: LineSegment StartX=-177.8 StartY=-127 StartZ=0 EndX=177.8 EndY=-127 EndZ=0
    g2: LineSegment StartX=177.8 StartY=-127 StartZ=0 EndX=177.8 EndY=127 EndZ=0
    g3: LineSegment StartX=177.8 StartY=127 StartZ=0 EndX=-177.8 EndY=127 EndZ=0
  constraints (11):
    c: Coincident(g0,g1)
    c: Coincident(g1,g2)
    c: Coincident(g2,g3)
    c: Coincident(g3,g0)
    c: Vertical(g0)
    c: Vertical(g2)
    c: Horizontal(g1)
    c: Horizontal(g3)
    c: DistanceY(g2,g2) = 254
    c: DistanceX(g3,g3) = 355.6
    c: Symmetric(g0,g1,g-1)
FEATURE [Sketcher::SketchObject] Sketch006  label="path001"
  ArcFitTolerance = 1e-06
  ExternalTypes = [0]
  FullyConstrained = true
  MakeInternals = false
  MapMode = 4
  Placement = pos=(0,0,0) rot=(1,0,0;1.5708rad)
  sketch-geometry (1):
    g0: LineSegment StartX=0 StartY=0 StartZ=0 EndX=304.8 EndY=0 EndZ=0
  constraints (3):
    c: Coincident(g0,g-1)
    c: PointOnObject(g0,g-1)
    c: DistanceX(g0,g0) = 304.8
FEATURE [Sketcher::SketchObject] Sketch005  label="round001"
  ArcFitTolerance = 1e-06
  AttachmentSupport = -> [Sketch006]
  ExternalTypes = [0]
  FullyConstrained = true
  MakeInternals = false
  MapMode = 1
  Placement = pos=(304.8,0,0) rot=(0.57735,0.57735,0.57735;2.0944rad)
  sketch-geometry (17):
    g0: LineSegment StartX=53.8815 StartY=53.8815 StartZ=0 EndX=29.1605 EndY=70.3996 EndZ=0
    g1: LineSegment StartX=29.1605 StartY=70.3996 StartZ=0 EndX=0 EndY=76.2 EndZ=0
    g2: LineSegment StartX=0 StartY=76.2 StartZ=0 EndX=-29.1605 EndY=70.3996 EndZ=0
    g3: LineSegment StartX=-29.1605 StartY=70.3996 StartZ=0 EndX=-53.8815 EndY=53.8815 EndZ=0
    g4: LineSegment StartX=-53.8815 StartY=53.8815 StartZ=0 EndX=-70.3996 EndY=29.1605 EndZ=0
    g5: LineSegment StartX=-70.3996 StartY=29.1605 StartZ=0 EndX=-76.2 EndY=-7.674e-13 EndZ=0
    g6: LineSegment StartX=-76.2 StartY=-7.674e-13 StartZ=0 EndX=-70.3996 EndY=-29.1605 EndZ=0
    g7: LineSegment StartX=-70.3996 StartY=-29.1605 StartZ=0 EndX=-53.8815 EndY=-53.8815 EndZ=0
    g8: LineSegment StartX=-53.8815 StartY=-53.8815 StartZ=0 EndX=-29.1605 EndY=-70.3996 EndZ=0
    g9: LineSegment StartX=-29.1605 StartY=-70.3996 StartZ=0 EndX=-1.137e-13 EndY=-76.2 EndZ=0
    g10: LineSegment StartX=-1.137e-13 StartY=-76.2 StartZ=0 EndX=29.1605 EndY=-70.3996 EndZ=0
    g11: LineSegment StartX=29.1605 StartY=-70.3996 StartZ=0 EndX=53.8815 EndY=-53.8815 EndZ=0
    g12: LineSegment StartX=53.8815 StartY=-53.8815 StartZ=0 EndX=70.3996 EndY=-29.1605 EndZ=0
    g13: LineSegment StartX=70.3996 StartY=-29.1605 StartZ=0 EndX=76.2 EndY=2.49e-14 EndZ=0
    g14: LineSegment StartX=76.2 StartY=2.49e-14 StartZ=0 EndX=70.3996 EndY=29.1605 EndZ=0
    g15: LineSegment StartX=70.3996 StartY=29.1605 StartZ=0 EndX=53.8815 EndY=53.8815 EndZ=0
    g16: Circle [constr] CenterX=0 CenterY=0 CenterZ=0 NormalX=0 NormalY=0 NormalZ=1 AngleXU=0 Radius=76.2
  constraints (36):
    c: Coincident(g0,g1)
    c: Coincident(g1,g2)
    c: Coincident(g2,g3)
    c: Coincident(g3,g4)
    c: Coincident(g4,g5)
    c: Coincident(g5,g6)
    c: Coincident(g6,g7)
    c: Coincident(g7,g8)
    c: Coincident(g8,g9)
    c: Coincident(g9,g10)
    c: Coincident(g10,g11)
    c: Coincident(g11,g12)
    c: Coincident(g12,g13)
    c: Coincident(g13,g14)
    c: Coincident(g14,g15)
    c: Coincident(g15,g0)
    c: Equal(g0, g1-g15) x15
    c: PointOnObject(g0,g16)
    c: PointOnObject(g1,g16)
    c: PointOnObject(g2,g16)
    c: PointOnObject(g3,g16)
    c: PointOnObject(g4,g16)
    c: PointOnObject(g5,g16)
    c: PointOnObject(g6,g16)
    c: PointOnObject(g7,g16)
    c: PointOnObject(g8,g16)
    c: PointOnObject(g9,g16)
    c: PointOnObject(g10,g16)
    c: PointOnObject(g11,g16)
    c: PointOnObject(g12,g16)
    c: PointOnObject(g13,g16)
    c: PointOnObject(g14,g16)
    c: PointOnObject(g15,g16)
    c: PointOnObject(g1,g-2)
    c: Diameter(g16) = 152.4
    c: Coincident(g16,g-1)
FEATURE [PartDesign::Body] Body002  label="developed"
  AllowCompound = false
  Group = -> [Sketch004,Sketch005,Sketch006]
  Origin = -> Origin002
FEATURE [App::Point] Origin003  label="Origin"
  Role = Origin
FEATURE [App::Point] Origin004  label="Origin"
  Role = Origin
FEATURE [App::Point] Origin005  label="Origin"
  Role = Origin
COMPONENT P3 — recipe-attached ("air-assist", a linked part whose construction recipe lives in a companion FreeCAD document of the same project; that document's serialized recipe follows).
Construction recipe (the companion document, serialized — sketch geometry with constraints, then the solid features built on it; lengths are millimeters unless a unit is written):

FCSTD DOCUMENT  (FreeCAD 1.0R39109 (Git))
Label: air-assist
License: All rights reserved
LicenseURL: http://en.wikipedia.org/wiki/All_rights_reserved
objects: Sketcher::SketchObject×2, PartDesign::Pad×2, PartDesign::Body×2, App::Part×1
note: 12 computed .brp shape members not serialized (recipe doc carries the construction recipe); baked Part::Feature solids carry a one-line shape summary decoded from their .brp

FEATURE [Sketcher::SketchObject] Sketch
  ArcFitTolerance = 0
  AttachmentSupport = -> [XZ_Plane]
  FullyConstrained = true
  MakeInternals = false
  MapMode = 5
  Placement = pos=(0,0,0) rot=(1,0,0;1.5708rad)
  sketch-geometry (10):
    g0: LineSegment StartX=-57.5 StartY=0 StartZ=0 EndX=-56.9739 EndY=35.9962 EndZ=0
    g1: LineSegment StartX=-56.9739 StartY=35.9962 StartZ=0 EndX=-51 EndY=38.8705 EndZ=0
    g2: LineSegment StartX=-51 StartY=38.8705 StartZ=0 EndX=-50.5 EndY=58.8643 EndZ=0
    g3: LineSegment StartX=-50.5 StartY=58.8643 StartZ=0 EndX=-31 EndY=78 EndZ=0
    g4: LineSegment StartX=-31 StartY=78 StartZ=0 EndX=31 EndY=78 EndZ=0
    g5: LineSegment StartX=31 StartY=78 StartZ=0 EndX=50.5 EndY=58.8643 EndZ=0
    g6: LineSegment StartX=50.5 StartY=58.8643 StartZ=0 EndX=51 EndY=38.8705 EndZ=0
    g7: LineSegment StartX=51 StartY=38.8705 StartZ=0 EndX=56.9739 EndY=35.9962 EndZ=0
    g8: LineSegment StartX=56.9739 StartY=35.9962 StartZ=0 EndX=57.5 EndY=0 EndZ=0
    g9: LineSegment StartX=57.5 StartY=0 StartZ=0 EndX=-57.5 EndY=0 EndZ=0
  constraints (25):
    c: PointOnObject(g0,g-1)
    c: Coincident(g0,g1)
    c: Coincident(g1,g2)
    c: Coincident(g2,g3)
    c: Coincident(g3,g4)
    c: Coincident(g4,g5)
    c: Coincident(g5,g6)
    c: Coincident(g6,g7)
    c: Coincident(g7,g8)
    c: Coincident(g8,g9)
    c: Coincident(g9,g0)
    c: Symmetric(g0,g8,g-2)
    c: DistanceX(g9,g9) = 115
    c: Symmetric(g1,g6,g-2)
    c: Symmetric(g3,g4,g-2)
    c: Symmetric(g2,g5,g-2)
    c: Symmetric(g0,g7,g-2)
    c: Distance(g8) = 36
    c: DistanceX(g4,g4) = 62
    c: DistanceX(g2,g5) = 101
    c: DistanceX(g1,g6) = 102
    c: Distance(g0,g8) = 120
    c: DistanceY(g0,g3) = 78
    c: Distance(g2,g8) = 123
    c: Distance(g6) = 20
FEATURE [PartDesign::Pad] Pad
  Direction = (0,-1,2e-16)
  Length = 76.962
  Length2 = 10
  Midplane = true
  Placement = pos=(0,0,0) rot=(1,0,0;1.5708rad)
  Profile = -> Sketch
  ReferenceAxis = -> Sketch [N_Axis]
  Suppressed = false
  Type = 0
FEATURE [PartDesign::Body] Body
  AllowCompound = false
  Group = -> [Sketch,Pad]
  Origin = -> Origin
  Tip = -> Pad
FEATURE [Sketcher::SketchObject] Sketch003
  ArcFitTolerance = 0
  FullyConstrained = true
  MakeInternals = false
  MapMode = 5
  Placement = pos=(0,0,0) rot=(1,0,0;1.5708rad)
  sketch-geometry (8):
    g0: LineSegment StartX=29 StartY=5 StartZ=0 EndX=-29 EndY=5 EndZ=0
    g1: LineSegment StartX=-34 StartY=10 StartZ=0 EndX=-34 EndY=65 EndZ=0
    g2: LineSegment StartX=-29 StartY=70 StartZ=0 EndX=29 EndY=70 EndZ=0
    g3: LineSegment StartX=34 StartY=65 StartZ=0 EndX=34 EndY=10 EndZ=0
    g4: ArcOfCircle CenterX=-29 CenterY=65 CenterZ=0 NormalX=0 NormalY=0 NormalZ=1 AngleXU=0 Radius=5 StartAngle=1.5708 EndAngle=3.14159
    g5: ArcOfCircle CenterX=-29 CenterY=10 CenterZ=0 NormalX=0 NormalY=0 NormalZ=1 AngleXU=0 Radius=5 StartAngle=3.14159 EndAngle=4.71239
    g6: ArcOfCircle CenterX=29 CenterY=10 CenterZ=0 NormalX=0 NormalY=0 NormalZ=1 AngleXU=0 Radius=5 StartAngle=4.71239 EndAngle=6.28319
    g7: ArcOfCircle CenterX=29 CenterY=65 CenterZ=0 NormalX=0 NormalY=0 NormalZ=1 AngleXU=0 Radius=5 StartAngle=6e-16 EndAngle=1.5708
  constraints (19):
    c: Horizontal(g0)
    c: Horizontal(g2)
    c: Vertical(g1)
    c: Vertical(g3)
    c: Tangent(g2,g4) = 1.5708
    c: Tangent(g1,g4) = 1.5708
    c: Tangent(g1,g5) = 1.5708
    c: Tangent(g0,g5) = 1.5708
    c: Tangent(g0,g6) = 1.5708
    c: Tangent(g3,g6) = 1.5708
    c: Tangent(g3,g7) = 1.5708
    c: Tangent(g2,g7) = 1.5708
    c: Equal(g7,g5)
    c: Equal(g7,g6)
    c: Radius(g7) = 5
    c: DistanceX(g1,g3) = 68
    c: DistanceY(g0,g2) = 65
    c: Symmetric(g1,g3,g-2)
    c: DistanceY(g-1,g0) = 5
FEATURE [PartDesign::Pad] Pad003
  Direction = (0,-1,2e-16)
  Length = 93
  Length2 = 10
  Midplane = true
  Placement = pos=(0,0,0) rot=(1,0,0;1.5708rad)
  Profile = -> Sketch003
  ReferenceAxis = -> Sketch003 [N_Axis]
  Suppressed = false
  Type = 0
FEATURE [PartDesign::Body] Body001
  AllowCompound = false
  Group = -> [Sketch003,Pad003]
  Origin = -> Origin001
  Tip = -> Pad003
FEATURE [App::Part] Part  label="air-assist"
  Group = -> [Body,Body001]
  Origin = -> Origin002
COMPONENT P4 — recipe-attached ("base", a linked part whose construction recipe lives in a companion FreeCAD document of the same project; that document's serialized recipe follows).
Construction recipe (the companion document, serialized — sketch geometry with constraints, then the solid features built on it; lengths are millimeters unless a unit is written):

FCSTD DOCUMENT  (FreeCAD 1.1R40971 (Git))
Label: base
License: All rights reserved
LicenseURL: http://en.wikipedia.org/wiki/All_rights_reserved
objects: Sketcher::SketchObject×4, PartDesign::Pad×4, App::Point×2, PartDesign::Body×1, App::Part×1
note: 21 computed .brp shape members not serialized (recipe doc carries the construction recipe); baked Part::Feature solids carry a one-line shape summary decoded from their .brp

FEATURE [Sketcher::SketchObject] Sketch  label="base-supportsk"
  ArcFitTolerance = 1e-06
  AttachmentSupport = -> [XY_Plane]
  ExternalTypes = [0]
  FullyConstrained = true
  MakeInternals = false
  MapMode = 5
  sketch-geometry (16):
    g0: LineSegment StartX=-520.7 StartY=317.5 StartZ=0 EndX=-520.7 EndY=279.4 EndZ=0
    g1: LineSegment StartX=-520.7 StartY=279.4 StartZ=0 EndX=-444.5 EndY=279.4 EndZ=0
    g2: LineSegment StartX=520.7 StartY=317.5 StartZ=0 EndX=-520.7 EndY=317.5 EndZ=0
    g3: LineSegment StartX=-520.7 StartY=-317.5 StartZ=0 EndX=-520.7 EndY=-279.4 EndZ=0
    g4: LineSegment StartX=-520.7 StartY=-279.4 StartZ=0 EndX=-444.5 EndY=-279.4 EndZ=0
    g5: LineSegment StartX=520.7 StartY=317.5 StartZ=0 EndX=520.7 EndY=-317.5 EndZ=0
    g6: LineSegment StartX=520.7 StartY=-317.5 StartZ=0 EndX=-520.7 EndY=-317.5 EndZ=0
    g7: LineSegment StartX=-444.5 StartY=279.4 StartZ=0 EndX=-444.5 EndY=-279.4 EndZ=0
    g8: LineSegment StartX=-406.4 StartY=-279.4 StartZ=0 EndX=-406.4 EndY=279.4 EndZ=0
    g9: LineSegment StartX=482.6 StartY=279.4 StartZ=0 EndX=482.6 EndY=-279.4 EndZ=0
    g10: LineSegment StartX=-406.4 StartY=279.4 StartZ=0 EndX=0 EndY=279.4 EndZ=0
    g11: LineSegment StartX=-406.4 StartY=-279.4 StartZ=0 EndX=0 EndY=-279.4 EndZ=0
    g12: LineSegment StartX=2e-15 StartY=279.4 StartZ=0 EndX=2e-15 EndY=-279.4 EndZ=0
    g13: LineSegment StartX=38.1 StartY=279.4 StartZ=0 EndX=38.1 EndY=-279.4 EndZ=0
    g14: LineSegment StartX=38.1 StartY=-279.4 StartZ=0 EndX=482.6 EndY=-279.4 EndZ=0
    g15: LineSegment StartX=38.1 StartY=279.4 StartZ=0 EndX=482.6 EndY=279.4 EndZ=0
  constraints (47):
    c: Coincident(g0,g1)
    c: Coincident(g2,g0)
    c: Vertical(g0)
    c: Horizontal(g1)
    c: Horizontal(g2)
    c: Coincident(g3,g4)
    c: Coincident(g5,g6)
    c: Coincident(g6,g3)
    c: Vertical(g3)
    c: Vertical(g5)
    c: Horizontal(g4)
    c: Horizontal(g6)
    c: Vertical(g7)
    c: Vertical(g8)
    c: Vertical(g9)
    c: DistanceX(g4,g5) = 1041.4
    c: DistanceY(g3,g0) = 635
    c: Symmetric(g5,g0,g-1)
    c: DistanceX(g0,g7) = 76.2
    c: DistanceY(g8,g8) = 558.8
    c: PointOnObject(g10,g8)
    c: Coincident(g14,g9)
    c: Coincident(g9,g15)
    c: Coincident(g8,g11)
    c: PointOnObject(g8,g1)
    c: PointOnObject(g8,g4)
    c: Coincident(g5,g2)
    c: Coincident(g7,g4)
    c: Coincident(g1,g7)
    c: Equal(g0,g3)
    c: DistanceY(g0,g0) = 38.1
    c: DistanceX(g1,g8) = 38.1
    c: DistanceX(g9,g2) = 38.1
    c: Vertical(g3,g0)
    c: Vertical(g12)
    c: Symmetric(g10,g15,g13)
    c: Symmetric(g11,g14,g13)
    c: Horizontal(g11)
    c: Horizontal(g14)
    c: Coincident(g12,g11)
    c: Coincident(g14,g13)
    c: PointOnObject(g8,g10)
    c: Horizontal(g10)
    c: Horizontal(g15)
    c: Coincident(g12,g10)
    c: Coincident(g15,g13)
    c: DistanceX(g10,g13) = 38.1
FEATURE [PartDesign::Pad] Pad  label="top"
  Direction = (0,0,1)
  Length = 88.9
  Length2 = 10
  Profile = -> Sketch
  ReferenceAxis = -> Sketch [N_Axis]
  Suppressed = false
  Type = 0
FEATURE [App::Point] Origin002  label="Origin"
  Role = Origin
FEATURE [App::Point] Origin003  label="Origin"
  Role = Origin
FEATURE [Sketcher::SketchObject] Sketch001  label="shelf-support-sk"
  ArcFitTolerance = 1e-06
  ExternalTypes = [0,0,0,0]
  FullyConstrained = true
  MakeInternals = false
  Placement = pos=(0,0,-406.4) rot=(0,0,1;0rad)
  sketch-geometry (20):
    g0: LineSegment StartX=-444.5 StartY=279.4 StartZ=0 EndX=-19.05 EndY=279.4 EndZ=0
    g1: LineSegment StartX=444.5 StartY=279.4 StartZ=0 EndX=444.5 EndY=317.5 EndZ=0
    g2: LineSegment StartX=444.5 StartY=317.5 StartZ=0 EndX=-444.5 EndY=317.5 EndZ=0
    g3: LineSegment StartX=-444.5 StartY=317.5 StartZ=0 EndX=-444.5 EndY=279.4 EndZ=0
    g4: LineSegment StartX=-444.5 StartY=-279.4 StartZ=0 EndX=-444.5 EndY=-317.5 EndZ=0
    g5: LineSegment StartX=-444.5 StartY=-317.5 StartZ=0 EndX=444.5 EndY=-317.5 EndZ=0
    g6: LineSegment StartX=444.5 StartY=-317.5 StartZ=0 EndX=444.5 EndY=-279.4 EndZ=0
    g7: LineSegment StartX=444.5 StartY=-279.4 StartZ=0 EndX=19.05 EndY=-279.4 EndZ=0
    g8: LineSegment StartX=-19.05 StartY=279.4 StartZ=0 EndX=-19.05 EndY=-279.4 EndZ=0
    g9: LineSegment StartX=19.05 StartY=-279.4 StartZ=0 EndX=19.05 EndY=279.4 EndZ=0
    g10: LineSegment StartX=19.05 StartY=279.4 StartZ=0 EndX=444.5 EndY=279.4 EndZ=0
    g11: LineSegment StartX=-19.05 StartY=-279.4 StartZ=0 EndX=-444.5 EndY=-279.4 EndZ=0
    g12: LineSegment StartX=-482.6 StartY=279.4 StartZ=0 EndX=-520.7 EndY=279.4 EndZ=0
    g13: LineSegment StartX=-520.7 StartY=279.4 StartZ=0 EndX=-520.7 EndY=-279.4 EndZ=0
    g14: LineSegment StartX=-520.7 StartY=-279.4 StartZ=0 EndX=-482.6 EndY=-279.4 EndZ=0
    g15: LineSegment StartX=-482.6 StartY=-279.4 StartZ=0 EndX=-482.6 EndY=279.4 EndZ=0
    g16: LineSegment StartX=482.6 StartY=279.4 StartZ=0 EndX=482.6 EndY=-279.4 EndZ=0
    g17: LineSegment StartX=482.6 StartY=-279.4 StartZ=0 EndX=520.7 EndY=-279.4 EndZ=0
    g18: LineSegment StartX=520.7 StartY=-279.4 StartZ=0 EndX=520.7 EndY=279.4 EndZ=0
    g19: LineSegment StartX=520.7 StartY=279.4 StartZ=0 EndX=482.6 EndY=279.4 EndZ=0
  constraints (58):
    c: Coincident(g10,g1)
    c: Coincident(g1,g2)
    c: Coincident(g2,g3)
    c: Coincident(g3,g0)
    c: Vertical(g1)
    c: Vertical(g3)
    c: DistanceY(g1,g1) = 38.1
    c: Coincident(g4,g5)
    c: Coincident(g5,g6)
    c: Coincident(g6,g7)
    c: Coincident(g11,g4)
    c: Vertical(g4)
    c: Vertical(g6)
    c: Horizontal(g5)
    c: Vertical(g8)
    c: Symmetric(g9,g8,g-2)
    c: Horizontal(g9,g10)
    c: Horizontal(g9,g6)
    c: DistanceX(g8,g9) = 38.1
    c: Equal(g1,g6)
    c: Symmetric(g9,g9,g-1)
    c: Symmetric(g2,g1,g-2)
    c: PointOnObject(g4,g3)
    c: PointOnObject(g6,g1)
    c: DistanceY(g4,g2) = 635
    c: Horizontal(g0)
    c: Coincident(g0,g8)
    c: Coincident(g10,g9)
    c: Horizontal(g11)
    c: Coincident(g7,g9)
    c: Coincident(g11,g8)
    c: Equal(g4,g1)
    c: Coincident(g12,g13)
    c: Coincident(g13,g14)
    c: Coincident(g14,g15)
    c: Coincident(g15,g12)
    c: Horizontal(g12)
    c: Horizontal(g14)
    c: Vertical(g13)
    c: Vertical(g15)
    c: Coincident(g16,g17)
    c: Coincident(g17,g18)
    c: Coincident(g18,g19)
    c: Coincident(g19,g16)
    c: Vertical(g16)
    c: Vertical(g18)
    c: Horizontal(g17)
    c: Horizontal(g19)
    c: Equal(g1,g19)
    c: Equal(g19,g12)
    c: PointOnObject(g12,g0)
    c: PointOnObject(g16,g7)
    c: PointOnObject(g14,g11)
    c: DistanceX(g12,g2) = 76.2
    c: DistanceX(g12,g18) = 1041.4
    c: DistanceX(g5,g5) = 889
    c: DistanceY(g15,g15) = 558.8
    c: Symmetric(g12,g18,g-2)
FEATURE [Sketcher::SketchObject] Sketch002  label="sklegs"
  ArcFitTolerance = 1e-06
  AttachmentSupport = -> [XY_Plane]
  ExternalGeometry = -> [Pad]
  ExternalTypes = [0,0,0,0,0]
  FullyConstrained = true
  MakeInternals = false
  MapMode = 5
  sketch-geometry (16):
    g0: LineSegment StartX=-520.7 StartY=317.5 StartZ=0 EndX=-520.7 EndY=279.4 EndZ=0
    g1: LineSegment StartX=-520.7 StartY=279.4 StartZ=0 EndX=-444.5 EndY=279.4 EndZ=0
    g2: LineSegment StartX=-444.5 StartY=279.4 StartZ=0 EndX=-444.5 EndY=317.5 EndZ=0
    g3: LineSegment StartX=-444.5 StartY=317.5 StartZ=0 EndX=-520.7 EndY=317.5 EndZ=0
    g4: LineSegment StartX=444.5 StartY=317.5 StartZ=0 EndX=444.5 EndY=279.4 EndZ=0
    g5: LineSegment StartX=444.5 StartY=279.4 StartZ=0 EndX=520.7 EndY=279.4 EndZ=0
    g6: LineSegment StartX=520.7 StartY=279.4 StartZ=0 EndX=520.7 EndY=317.5 EndZ=0
    g7: LineSegment StartX=520.7 StartY=317.5 StartZ=0 EndX=444.5 EndY=317.5 EndZ=0
    g8: LineSegment StartX=520.7 StartY=-279.4 StartZ=0 EndX=444.5 EndY=-279.4 EndZ=0
    g9: LineSegment StartX=444.5 StartY=-279.4 StartZ=0 EndX=444.5 EndY=-317.5 EndZ=0
    g10: LineSegment StartX=444.5 StartY=-317.5 StartZ=0 EndX=520.7 EndY=-317.5 EndZ=0
    g11: LineSegment StartX=520.7 StartY=-317.5 StartZ=0 EndX=520.7 EndY=-279.4 EndZ=0
    g12: LineSegment StartX=-444.5 StartY=-279.4 StartZ=0 EndX=-520.7 EndY=-279.4 EndZ=0
    g13: LineSegment StartX=-520.7 StartY=-279.4 StartZ=0 EndX=-520.7 EndY=-317.5 EndZ=0
    g14: LineSegment StartX=-520.7 StartY=-317.5 StartZ=0 EndX=-444.5 EndY=-317.5 EndZ=0
    g15: LineSegment StartX=-444.5 StartY=-317.5 StartZ=0 EndX=-444.5 EndY=-279.4 EndZ=0
  constraints (43):
    c: Coincident(g0,g1)
    c: Coincident(g1,g2)
    c: Coincident(g2,g3)
    c: Coincident(g3,g0)
    c: Vertical(g2)
    c: Horizontal(g1)
    c: Horizontal(g3)
    c: Coincident(g4,g5)
    c: Coincident(g5,g6)
    c: Coincident(g6,g7)
    c: Coincident(g7,g4)
    c: Vertical(g4)
    c: Vertical(g6)
    c: Horizontal(g5)
    c: Horizontal(g7)
    c: Coincident(g8,g9)
    c: Coincident(g9,g10)
    c: Coincident(g10,g11)
    c: Coincident(g11,g8)
    c: Horizontal(g8)
    c: Horizontal(g10)
    c: Vertical(g9)
    c: Vertical(g11)
    c: Coincident(g12,g13)
    c: Coincident(g13,g14)
    c: Coincident(g14,g15)
    c: Coincident(g15,g12)
    c: Horizontal(g12)
    c: Horizontal(g14)
    c: Vertical(g13)
    c: Vertical(g15)
    c: Coincident(g0,g-3)
    c: Coincident(g-5,g0)
    c: Horizontal(g5,g0)
    c: Coincident(g13,g-6)
    c: Coincident(g10,g-7)
    c: Vertical(g4,g8)
    c: Vertical(g12,g1)
    c: Coincident(g6,g-4)
    c: Equal(g5,g1)
    c: Equal(g15,g9)
    c: Equal(g9,g0)
    c: DistanceX(g0,g1) = 76.2
FEATURE [PartDesign::Pad] Pad003
  BaseFeature = -> Pad
  Direction = (0,0,1)
  Length = 914.4
  Length2 = 10
  Profile = -> Sketch002
  ReferenceAxis = -> Sketch002 [N_Axis]
  Reversed = true
  Suppressed = false
  Type = 0
FEATURE [PartDesign::Pad] Pad004
  BaseFeature = -> Pad003
  Direction = (0,0,1)
  Length = 76.2
  Length2 = 10
  Profile = -> Sketch001
  ReferenceAxis = -> Sketch001 [N_Axis]
  Reversed = true
  Suppressed = false
  Type = 0
FEATURE [Sketcher::SketchObject] Sketch003  label="skshelf"
  ArcFitTolerance = 1e-06
  ExternalTypes = [0,0]
  FullyConstrained = true
  MakeInternals = false
  MapMode = 5
  Placement = pos=(0,0,-406.4) rot=(0,0,1;0rad)
  sketch-geometry (4):
    g0: LineSegment StartX=-520.7 StartY=317.5 StartZ=0 EndX=-520.7 EndY=-317.5 EndZ=0
    g1: LineSegment StartX=-520.7 StartY=-317.5 StartZ=0 EndX=520.7 EndY=-317.5 EndZ=0
    g2: LineSegment StartX=520.7 StartY=-317.5 StartZ=0 EndX=520.7 EndY=317.5 EndZ=0
    g3: LineSegment StartX=520.7 StartY=317.5 StartZ=0 EndX=-520.7 EndY=317.5 EndZ=0
  constraints (11):
    c: Coincident(g0,g1)
    c: Coincident(g1,g2)
    c: Coincident(g2,g3)
    c: Coincident(g3,g0)
    c: Vertical(g0)
    c: Vertical(g2)
    c: Horizontal(g1)
    c: Horizontal(g3)
    c: DistanceX(g3,g3) = 1041.4
    c: DistanceY(g2,g2) = 635
    c: Symmetric(g2,g0,g-1)
FEATURE [PartDesign::Pad] Pad005
  BaseFeature = -> Pad004
  Direction = (0,0,1)
  Length = 12.7
  Length2 = 10
  Profile = -> Sketch003
  ReferenceAxis = -> Sketch003 [N_Axis]
  Suppressed = false
  Type = 0
FEATURE [PartDesign::Body] Body  label="base"
  AllowCompound = false
  Group = -> [Pad,Sketch,Sketch002,Pad003,Sketch001,Pad004,Sketch003,Pad005]
  Origin = -> Origin
  Tip = -> Pad005
FEATURE [App::Part] Part
  Group = -> [Body]
  Origin = -> Origin001
COMPONENT P5 — recipe-attached ("elbow", a linked part whose construction recipe lives in a companion FreeCAD document of the same project; that document's serialized recipe follows).
Construction recipe (the companion document, serialized — sketch geometry with constraints, then the solid features built on it; lengths are millimeters unless a unit is written):

FCSTD DOCUMENT  (FreeCAD 1.1R40971 (Git))
Label: elbow
License: All rights reserved
LicenseURL: http://en.wikipedia.org/wiki/All_rights_reserved
objects: Sketcher::SketchObject×2, PartDesign::Pad×1, PartDesign::Pocket×1, App::Point×1, PartDesign::Thickness×1, PartDesign::Body×1
note: 14 computed .brp shape members not serialized (recipe doc carries the construction recipe); baked Part::Feature solids carry a one-line shape summary decoded from their .brp

FEATURE [Sketcher::SketchObject] Sketch001  label="elbowsk"
  ArcFitTolerance = 1e-06
  AttachmentSupport = -> [XZ_Plane]
  ExternalTypes = [0]
  FullyConstrained = false
  MakeInternals = false
  MapMode = 5
  Placement = pos=(0,0,0) rot=(1,0,0;1.5708rad)
  sketch-geometry (18):
    g0: LineSegment StartX=279.4 StartY=-234.95 StartZ=0 EndX=279.4 EndY=-488.95 EndZ=0
    g1: LineSegment [constr] StartX=279.4 StartY=-234.95 StartZ=0 EndX=558.8 EndY=-292.581 EndZ=0
    g2: LineSegment [constr] StartX=558.8 StartY=-292.581 StartZ=0 EndX=558.8 EndY=-444.981 EndZ=0
    g3: LineSegment [constr] StartX=558.8 StartY=-444.981 StartZ=0 EndX=279.4 EndY=-488.95 EndZ=0
    g4: LineSegment [constr] StartX=279.4 StartY=-361.95 StartZ=0 EndX=558.8 EndY=-371.348 EndZ=0
    g5: LineSegment StartX=0 StartY=-107.95 StartZ=0 EndX=73.152 EndY=-107.95 EndZ=0
    g6: Circle [constr] CenterX=0 CenterY=-107.95 CenterZ=0 NormalX=0 NormalY=0 NormalZ=1 AngleXU=0 Radius=1
    g7: Circle [constr] CenterX=0 CenterY=-488.95 CenterZ=0 NormalX=0 NormalY=0 NormalZ=1 AngleXU=0 Radius=1
    g8: Circle [constr] CenterX=279.4 CenterY=-488.95 CenterZ=0 NormalX=0 NormalY=0 NormalZ=1 AngleXU=0 Radius=1
    g9: BSplineCurve PolesCount=3 KnotsCount=2 Degree=2 IsPeriodic=0
    g10: GeomPoint [constr] X=0 Y=-107.95 Z=0
    g11: GeomPoint [constr] X=279.4 Y=-488.95 Z=0
    g12: Circle [constr] CenterX=73.152 CenterY=-107.95 CenterZ=0 NormalX=0 NormalY=0 NormalZ=1 AngleXU=0 Radius=1
    g13: Circle [constr] CenterX=73.152 CenterY=-199.743 CenterZ=0 NormalX=0 NormalY=0 NormalZ=1 AngleXU=0 Radius=1
    g14: Circle [constr] CenterX=279.4 CenterY=-234.95 CenterZ=0 NormalX=0 NormalY=0 NormalZ=1 AngleXU=0 Radius=1
    g15: BSplineCurve PolesCount=3 KnotsCount=2 Degree=2 IsPeriodic=0
    g16: GeomPoint [constr] X=73.152 Y=-107.95 Z=0
    g17: GeomPoint [constr] X=279.4 Y=-234.95 Z=0
  constraints (43):
    c: Vertical(g0)
    c: DistanceY(g0,g0) = 254
    c: Vertical(g2)
    c: DistanceX(g3,g3) = 279.4
    c: Coincident(g2,g3)
    c: Coincident(g1,g2)
    c: Coincident(g1,g0)
    c: DistanceY(g2,g1) = 152.4
    c: PointOnObject(g4,g2)
    c: Symmetric(g0,g0,g4)
    c: Horizontal(g5)
    c: DistanceY(g5,g-1) = 107.95
    c: DistanceX(g5,g5) = 73.152
    c: DistanceX(g5,g2) = 558.8
    c: Vertical(g5,g-1)
    c: Weight(g6) = 1
    c: Equal(g6,g7)
    c: Equal(g6,g8)
    c: InternalAlignment(g6,g9)
    c: InternalAlignment(g7,g9)
    c: InternalAlignment(g8,g9)
    c: InternalAlignment(g10,g9)
    c: InternalAlignment(g11,g9)
    c: Coincident(g6,g5)
    c: Coincident(g8,g0)
    c: Weight(g12) = 1
    c: Equal(g12,g13)
    c: Equal(g12,g14)
    c: InternalAlignment(g12,g15)
    c: InternalAlignment(g13,g15)
    c: InternalAlignment(g14,g15)
    c: InternalAlignment(g16,g15)
    c: InternalAlignment(g17,g15)
    c: Coincident(g12,g5)
    c: Coincident(g14,g0)
    c: DistanceY(g9,g4) = 117.602
    c: DistanceY(g9,g9) = 381
    c: DistanceX(g9,g9) = 279.4
    c: PointOnObject(g7,g-2)
    c: Vertical(g13,g15)
    c: Horizontal(g7,g9)
    c: Coincident(g9,g3)
    c: DistanceY(g4,g4) = 9.398
FEATURE [PartDesign::Pad] Pad
  Direction = (0,-1,2e-16)
  Length = 558.8
  Length2 = 10
  Midplane = true
  Placement = pos=(0,0,0) rot=(1,0,0;1.5708rad)
  Profile = -> Sketch001
  ReferenceAxis = -> Sketch001 [N_Axis]
  Suppressed = false
  Type = 0
FEATURE [Sketcher::SketchObject] Sketch005  label="straightwall"
  ArcFitTolerance = 1e-06
  AttachmentSupport = -> [XY_Plane]
  ExternalTypes = [0]
  FullyConstrained = true
  MakeInternals = false
  MapMode = 5
  sketch-geometry (17):
    g0: LineSegment StartX=73.152 StartY=279.4 StartZ=0 EndX=279.4 EndY=152.4 EndZ=0
    g1: LineSegment StartX=279.4 StartY=152.4 StartZ=0 EndX=279.4 EndY=-152.4 EndZ=0
    g2: LineSegment StartX=279.4 StartY=-152.4 StartZ=0 EndX=73.152 EndY=-279.4 EndZ=0
    g3: LineSegment StartX=73.152 StartY=-317.5 StartZ=0 EndX=352.552 EndY=-317.5 EndZ=0
    g4: LineSegment StartX=352.552 StartY=-317.5 StartZ=0 EndX=352.552 EndY=317.5 EndZ=0
    g5: LineSegment StartX=352.552 StartY=317.5 StartZ=0 EndX=73.152 EndY=317.5 EndZ=0
    g6: LineSegment [constr] StartX=73.152 StartY=279.4 StartZ=0 EndX=73.152 EndY=-279.4 EndZ=0
    g7: LineSegment StartX=73.152 StartY=279.4 StartZ=0 EndX=11.2776 EndY=317.5 EndZ=0
    g8: LineSegment StartX=73.152 StartY=317.5 StartZ=0 EndX=11.2776 EndY=317.5 EndZ=0
    g9: LineSegment StartX=73.152 StartY=-279.4 StartZ=0 EndX=11.2776 EndY=-317.5 EndZ=0
    g10: LineSegment StartX=11.2776 StartY=-317.5 StartZ=0 EndX=73.152 EndY=-317.5 EndZ=0
    g11: LineSegment [constr] StartX=0 StartY=317.5 StartZ=0 EndX=0 EndY=-317.5 EndZ=0
    g12: LineSegment [constr] StartX=0 StartY=279.4 StartZ=0 EndX=352.552 EndY=279.4 EndZ=0
    g13: LineSegment [constr] StartX=279.4 StartY=152.4 StartZ=0 EndX=558.8 EndY=76.2 EndZ=0
    g14: LineSegment [constr] StartX=558.8 StartY=76.2 StartZ=0 EndX=558.8 EndY=-76.2 EndZ=0
    g15: LineSegment [constr] StartX=558.8 StartY=-76.2 StartZ=0 EndX=279.4 EndY=-152.4 EndZ=0
    g16: LineSegment [constr] StartX=0 StartY=0 StartZ=0 EndX=558.8 EndY=0 EndZ=0
  constraints (49):
    c: Coincident(g0,g1)
    c: Coincident(g1,g2)
    c: DistanceY(g1,g1) = 304.8
    c: Symmetric(g0,g1,g-1)
    c: Symmetric(g2,g0,g-1)
    c: Coincident(g3,g4)
    c: Coincident(g4,g5)
    c: Horizontal(g3)
    c: Symmetric(g4,g3,g-1)
    c: DistanceY(g4,g4) = 635
    c: Vertical(g0,g3)
    c: Vertical(g5,g0)
    c: Horizontal(g5)
    c: Angle(g2,g-2) = 1.01887
    c: Coincident(g6,g0)
    c: Coincident(g6,g2)
    c: Coincident(g7,g0)
    c: Coincident(g8,g5)
    c: Coincident(g8,g7)
    c: Coincident(g9,g2)
    c: Coincident(g10,g9)
    c: Coincident(g10,g3)
    c: Horizontal(g10)
    c: Parallel(g9,g2)
    c: Horizontal(g8)
    c: Parallel(g7,g0)
    c: Vertical(g11)
    c: PointOnObject(g11,g10)
    c: PointOnObject(g11,g8)
    c: DistanceX(g11,g0) = 73.152
    c: PointOnObject(g11,g-2)
    c: DistanceX(g5,g5) = 279.4
    c: PointOnObject(g12,g11)
    c: PointOnObject(g12,g4)
    c: Horizontal(g12)
    c: DistanceY(g12,g4) = 38.1
    c: DistanceY(g2,g0) = 558.8
    c: DistanceX(g12,g0) = 279.4
    c: Coincident(g13,g0)
    c: Vertical(g14)
    c: Coincident(g15,g1)
    c: DistanceX(g1,g14) = 279.4
    c: DistanceX(g11,g14) = 558.8
    c: Coincident(g14,g15)
    c: Coincident(g14,g13)
    c: DistanceY(g14,g14) = 152.4
    c: Coincident(g16,g-1)
    c: Horizontal(g16)
    c: Symmetric(g14,g13,g16)
FEATURE [PartDesign::Pocket] Pocket
  BaseFeature = -> Pad
  Direction = (0,0,-1)
  Length = 5
  Length2 = 5
  Placement = pos=(0,0,0) rot=(1,0,0;1.5708rad)
  Profile = -> Sketch005
  ReferenceAxis = -> Sketch005 [N_Axis]
  Suppressed = false
  Type = 1
FEATURE [App::Point] Origin001  label="Origin"
  Role = Origin
FEATURE [PartDesign::Thickness] Thickness
  Base = -> Pocket [Face8,Face1]
  BaseFeature = -> Pocket
  Intersection = true
  Join = 1
  Mode = 1
  Reversed = true
  SupportTransform = false
  Suppressed = false
  Value = 3.302
FEATURE [PartDesign::Body] Body  label="elbow"
  AllowCompound = false
  Group = -> [Sketch001,Pad,Sketch005,Pocket,Thickness]
  Origin = -> Origin
  Tip = -> Thickness
COMPONENT P6 — recipe-attached ("enclosure", a linked part whose construction recipe lives in a companion FreeCAD document of the same project; that document's serialized recipe follows).
Construction recipe (the companion document, serialized — sketch geometry with constraints, then the solid features built on it; lengths are millimeters unless a unit is written):

FCSTD DOCUMENT  (FreeCAD 1.1R40971 (Git))
Label: enclosure
License: All rights reserved
LicenseURL: http://en.wikipedia.org/wiki/All_rights_reserved
objects: Sketcher::SketchObject×6, PartDesign::Pad×6, App::Point×6, PartDesign::Body×5, App::Part×1
note: 35 computed .brp shape members not serialized (recipe doc carries the construction recipe); baked Part::Feature solids carry a one-line shape summary decoded from their .brp

FEATURE [Sketcher::SketchObject] Sketch
  ArcFitTolerance = 1e-06
  ExternalTypes = [0]
  FullyConstrained = true
  MakeInternals = false
  sketch-geometry (5):
    g0: LineSegment [constr] StartX=-520.7 StartY=304.8 StartZ=0 EndX=-520.7 EndY=-304.8 EndZ=0
    g1: LineSegment StartX=-444.5 StartY=-304.8 StartZ=0 EndX=520.7 EndY=-304.8 EndZ=0
    g2: LineSegment StartX=520.7 StartY=-304.8 StartZ=0 EndX=520.7 EndY=304.8 EndZ=0
    g3: LineSegment StartX=-444.5 StartY=-304.8 StartZ=0 EndX=-444.5 EndY=304.8 EndZ=0
    g4: LineSegment StartX=-444.5 StartY=304.8 StartZ=0 EndX=520.7 EndY=304.8 EndZ=0
  constraints (16):
    c: Coincident(g3,g4)
    c: Coincident(g1,g3)
    c: PointOnObject(g0,g1)
    c: DistanceX(g1,g1) = 965.2
    c: DistanceY(g2,g2) = 609.6
    c: DistanceX(g0,g1) = 76.2
    c: Vertical(g3)
    c: Vertical(g0)
    c: Coincident(g4,g2)
    c: Horizontal(g4)
    c: Coincident(g2,g1)
    c: PointOnObject(g0,g4)
    c: Symmetric(g1,g0,g-2)
    c: DistanceX(g3,g-1) = 444.5
    c: DistanceX(g0,g-1) = 520.7
    c: Symmetric(g1,g2,g-1)
FEATURE [PartDesign::Pad] Pad
  Direction = (0,0,1)
  Length = 20.32
  Length2 = 10
  Profile = -> Sketch
  ReferenceAxis = -> Sketch [N_Axis]
  Suppressed = false
  Type = 0
FEATURE [PartDesign::Body] Body  label="pad"
  AllowCompound = false
  Group = -> [Sketch,Pad]
  Origin = -> Origin
  Placement = pos=(-0.00178528,0.0656084,0.576416) rot=(0,0,1;0rad)
  Tip = -> Pad
FEATURE [Sketcher::SketchObject] Sketch004  label="outer-sk"
  ArcFitTolerance = 1e-06
  ExternalTypes = [0]
  FullyConstrained = true
  MakeInternals = false
  MapMode = 5
  Placement = pos=(0,-311.15,0) rot=(1,0,0;1.5708rad)
  sketch-geometry (13):
    g0: LineSegment StartX=-520.7 StartY=304.8 StartZ=0 EndX=-520.7 EndY=0 EndZ=0
    g1: LineSegment StartX=-520.7 StartY=0 StartZ=0 EndX=520.7 EndY=0 EndZ=0
    g2: LineSegment StartX=520.7 StartY=0 StartZ=0 EndX=520.7 EndY=304.8 EndZ=0
    g3: LineSegment StartX=520.7 StartY=304.8 StartZ=0 EndX=-520.7 EndY=304.8 EndZ=0
    g4: LineSegment StartX=-447.675 StartY=95.25 StartZ=0 EndX=-447.675 EndY=38.1 EndZ=0
    g5: LineSegment StartX=-447.675 StartY=38.1 StartZ=0 EndX=441.325 EndY=38.1 EndZ=0
    g6: LineSegment StartX=441.325 StartY=38.1 StartZ=0 EndX=441.325 EndY=95.25 EndZ=0
    g7: LineSegment StartX=441.325 StartY=95.25 StartZ=0 EndX=-447.675 EndY=95.25 EndZ=0
    g8: LineSegment [constr] StartX=517.525 StartY=304.8 StartZ=0 EndX=517.525 EndY=0 EndZ=0
    g9: LineSegment [constr] StartX=-517.525 StartY=304.8 StartZ=0 EndX=-517.525 EndY=0 EndZ=0
    g10: LineSegment [constr] StartX=-447.675 StartY=38.1 StartZ=0 EndX=-447.675 EndY=0 EndZ=0
    g11: LineSegment [constr] StartX=-447.675 StartY=50.8 StartZ=0 EndX=441.325 EndY=50.8 EndZ=0
    g12: LineSegment [constr] StartX=441.325 StartY=82.55 StartZ=0 EndX=-447.675 EndY=82.55 EndZ=0
  constraints (43):
    c: Coincident(g0,g1)
    c: Coincident(g1,g2)
    c: Coincident(g2,g3)
    c: Coincident(g3,g0)
    c: Vertical(g0)
    c: Vertical(g2)
    c: Horizontal(g1)
    c: PointOnObject(g1,g-1)
    c: DistanceX(g3,g3) = 1041.4
    c: Coincident(g4,g5)
    c: Coincident(g5,g6)
    c: Coincident(g6,g7)
    c: Coincident(g7,g4)
    c: Vertical(g4)
    c: Vertical(g6)
    c: Horizontal(g5)
    c: Horizontal(g7)
    c: DistanceX(g7,g7) = 889
    c: DistanceY(g-1,g0) = 304.8
    c: DistanceY(g4,g6) = 57.15
    c: Symmetric(g2,g0,g-2)
    c: PointOnObject(g8,g3)
    c: PointOnObject(g8,g1)
    c: Vertical(g8)
    c: DistanceX(g8,g1) = 3.175
    c: PointOnObject(g9,g1)
    c: Vertical(g9)
    c: Symmetric(g9,g8,g-2)
    c: PointOnObject(g10,g5)
    c: PointOnObject(g10,g1)
    c: Vertical(g10)
    c: DistanceX(g10,g8) = 965.2
    c: DistanceX(g9,g10) = 69.85
    c: DistanceX(g9,g4) = 69.85
    c: PointOnObject(g11,g4)
    c: PointOnObject(g11,g6)
    c: Horizontal(g11)
    c: PointOnObject(g12,g6)
    c: PointOnObject(g12,g4)
    c: Horizontal(g12)
    c: DistanceY(g11,g12) = 31.75
    c: DistanceY(g10,g11) = 50.8
    c: DistanceY(g10,g11) = 12.7
FEATURE [PartDesign::Pad] Pad002  label="outer"
  Direction = (0,-1,-2e-16)
  Length = 2.54
  Length2 = 10
  Placement = pos=(0,-311.15,0) rot=(1,0,0;1.5708rad)
  Profile = -> Sketch004
  ReferenceAxis = -> Sketch004 [N_Axis]
  Suppressed = false
  Type = 0
FEATURE [Sketcher::SketchObject] Sketch005  label="magnet-holder"
  ArcFitTolerance = 1e-06
  ExternalTypes = [0]
  FullyConstrained = true
  MakeInternals = false
  MapMode = 5
  Placement = pos=(0,-311.15,0) rot=(1,0,0;1.5708rad)
  sketch-geometry (43):
    g0: LineSegment StartX=-447.675 StartY=0 StartZ=0 EndX=-447.675 EndY=50.8 EndZ=0
    g1: LineSegment StartX=-447.675 StartY=82.55 StartZ=0 EndX=441.325 EndY=82.55 EndZ=0
    g2: LineSegment StartX=441.325 StartY=50.8 StartZ=0 EndX=441.325 EndY=0 EndZ=0
    g3: LineSegment StartX=441.325 StartY=0 StartZ=0 EndX=-447.675 EndY=0 EndZ=0
    g4: LineSegment StartX=-447.675 StartY=82.55 StartZ=0 EndX=-447.675 EndY=133.35 EndZ=0
    g5: LineSegment StartX=-447.675 StartY=133.35 StartZ=0 EndX=441.325 EndY=133.35 EndZ=0
    g6: LineSegment StartX=441.325 StartY=133.35 StartZ=0 EndX=441.325 EndY=82.55 EndZ=0
    g7: LineSegment StartX=441.325 StartY=50.8 StartZ=0 EndX=-447.675 EndY=50.8 EndZ=0
    g8: LineSegment [constr] StartX=-447.675 StartY=89.662 StartZ=0 EndX=441.325 EndY=89.662 EndZ=0
    g9: LineSegment [constr] StartX=441.325 StartY=44.45 StartZ=0 EndX=-447.675 EndY=44.45 EndZ=0
    g10: Circle CenterX=-422.275 CenterY=89.662 CenterZ=0 NormalX=0 NormalY=0 NormalZ=1 AngleXU=0 Radius=4.953
    g11: Circle CenterX=-302.532 CenterY=89.662 CenterZ=0 NormalX=0 NormalY=0 NormalZ=1 AngleXU=0 Radius=4.953
    g12: Circle CenterX=-182.789 CenterY=89.662 CenterZ=0 NormalX=0 NormalY=0 NormalZ=1 AngleXU=0 Radius=4.953
    g13: Circle CenterX=-63.0464 CenterY=89.662 CenterZ=0 NormalX=0 NormalY=0 NormalZ=1 AngleXU=0 Radius=4.953
    g14: Circle CenterX=56.6964 CenterY=89.662 CenterZ=0 NormalX=0 NormalY=0 NormalZ=1 AngleXU=0 Radius=4.953
    g15: Circle CenterX=176.439 CenterY=89.662 CenterZ=0 NormalX=0 NormalY=0 NormalZ=1 AngleXU=0 Radius=4.953
    g16: Circle CenterX=296.182 CenterY=89.662 CenterZ=0 NormalX=0 NormalY=0 NormalZ=1 AngleXU=0 Radius=4.953
    g17: Circle CenterX=415.925 CenterY=89.662 CenterZ=0 NormalX=0 NormalY=0 NormalZ=1 AngleXU=0 Radius=4.953
    g18: LineSegment [constr] StartX=-422.275 StartY=89.662 StartZ=0 EndX=-302.532 EndY=89.662 EndZ=0
    g19: LineSegment [constr] StartX=-302.532 StartY=89.662 StartZ=0 EndX=-182.789 EndY=89.662 EndZ=0
    g20: LineSegment [constr] StartX=-182.789 StartY=89.662 StartZ=0 EndX=-63.0464 EndY=89.662 EndZ=0
    g21: LineSegment [constr] StartX=-63.0464 StartY=89.662 StartZ=0 EndX=56.6964 EndY=89.662 EndZ=0
    g22: LineSegment [constr] StartX=56.6964 StartY=89.662 StartZ=0 EndX=176.439 EndY=89.662 EndZ=0
    g23: LineSegment [constr] StartX=176.439 StartY=89.662 StartZ=0 EndX=296.182 EndY=89.662 EndZ=0
    g24: LineSegment [constr] StartX=296.182 StartY=89.662 StartZ=0 EndX=415.925 EndY=89.662 EndZ=0
    g25: GeomPoint [constr] X=-3.175 Y=89.662 Z=0
    g26: Circle CenterX=-422.275 CenterY=44.45 CenterZ=0 NormalX=0 NormalY=0 NormalZ=1 AngleXU=0 Radius=4.953
    g27: Circle CenterX=-302.532 CenterY=44.45 CenterZ=0 NormalX=0 NormalY=0 NormalZ=1 AngleXU=0 Radius=4.953
    g28: Circle CenterX=-182.789 CenterY=44.45 CenterZ=0 NormalX=0 NormalY=0 NormalZ=1 AngleXU=0 Radius=4.953
    g29: Circle CenterX=-63.0464 CenterY=44.45 CenterZ=0 NormalX=0 NormalY=0 NormalZ=1 AngleXU=0 Radius=4.953
    g30: Circle CenterX=56.6964 CenterY=44.45 CenterZ=0 NormalX=0 NormalY=0 NormalZ=1 AngleXU=0 Radius=4.953
    g31: Circle CenterX=176.439 CenterY=44.45 CenterZ=0 NormalX=0 NormalY=0 NormalZ=1 AngleXU=0 Radius=4.953
    g32: Circle CenterX=296.182 CenterY=44.45 CenterZ=0 NormalX=0 NormalY=0 NormalZ=1 AngleXU=0 Radius=4.953
    g33: Circle CenterX=415.925 CenterY=44.45 CenterZ=0 NormalX=0 NormalY=0 NormalZ=1 AngleXU=0 Radius=4.953
    g34: LineSegment [constr] StartX=-422.275 StartY=44.45 StartZ=0 EndX=-302.532 EndY=44.45 EndZ=0
    g35: LineSegment [constr] StartX=-302.532 StartY=44.45 StartZ=0 EndX=-182.789 EndY=44.45 EndZ=0
    g36: LineSegment [constr] StartX=-182.789 StartY=44.45 StartZ=0 EndX=-63.0464 EndY=44.45 EndZ=0
    g37: LineSegment [constr] StartX=-63.0464 StartY=44.45 StartZ=0 EndX=56.6964 EndY=44.45 EndZ=0
    g38: LineSegment [constr] StartX=56.6964 StartY=44.45 StartZ=0 EndX=176.439 EndY=44.45 EndZ=0
    g39: LineSegment [constr] StartX=176.439 StartY=44.45 StartZ=0 EndX=296.182 EndY=44.45 EndZ=0
    g40: LineSegment [constr] StartX=296.182 StartY=44.45 StartZ=0 EndX=415.925 EndY=44.45 EndZ=0
    g41: LineSegment [constr] StartX=-517.525 StartY=304.8 StartZ=0 EndX=-517.525 EndY=0 EndZ=0
    g42: LineSegment [constr] StartX=517.525 StartY=304.8 StartZ=0 EndX=517.525 EndY=0 EndZ=0
  constraints (117):
    c: Coincident(g2,g3)
    c: Coincident(g3,g0)
    c: Vertical(g0)
    c: Vertical(g2)
    c: Horizontal(g1)
    c: Horizontal(g3)
    c: PointOnObject(g0,g-1)
    c: Coincident(g4,g5)
    c: Coincident(g5,g6)
    c: Vertical(g4)
    c: Vertical(g6)
    c: Horizontal(g5)
    c: Horizontal(g7)
    c: PointOnObject(g7,g2)
    c: DistanceY(g7,g1) = 31.75
    c: DistanceX(g3,g3) = 889
    c: PointOnObject(g9,g4)
    c: Horizontal(g9)
    c: Horizontal(g8)
    c: PointOnObject(g8,g0)
    c: PointOnObject(g8,g2)
    c: PointOnObject(g9,g2)
    c: DistanceY(g1,g8) = 7.112
    c: DistanceY(g9,g7) = 6.35
    c: Diameter(g10) = 9.906
    c: Coincident(g18,g10)
    c: Coincident(g18,g11)
    c: Horizontal(g18)
    c: Coincident(g19,g11)
    c: Coincident(g19,g12)
    c: Horizontal(g19)
    c: Coincident(g20,g12)
    c: Coincident(g20,g13)
    c: Horizontal(g20)
    c: Coincident(g21,g13)
    c: Coincident(g21,g14)
    c: Horizontal(g21)
    c: Coincident(g22,g14)
    c: Horizontal(g22)
    c: Coincident(g23,g15)
    c: Coincident(g23,g16)
    c: Horizontal(g23)
    c: Coincident(g24,g16)
    c: Coincident(g24,g17)
    c: Horizontal(g24)
    c: Equal(g24,g23)
    c: Equal(g23,g22)
    c: Equal(g22,g21)
    c: Equal(g21,g20)
    c: Equal(g20,g19)
    c: Equal(g19,g18)
    c: DistanceX(g10,g17) = 838.2
    c: Coincident(g22,g15)
    c: Equal(g17,g16)
    c: Equal(g16,g15)
    c: Equal(g15,g14)
    c: Equal(g14,g13)
    c: Equal(g13,g12)
    c: Equal(g12,g11)
    c: Equal(g11,g10)
    c: Symmetric(g21,g21,g25)
    c: Symmetric(g8,g8,g25)
    c: Equal(g26,g10)
    c: Coincident(g34,g26)
    c: Coincident(g34,g27)
    c: Horizontal(g34)
    c: Coincident(g35,g27)
    c: Coincident(g35,g28)
    c: Horizontal(g35)
    c: Coincident(g36,g28)
    c: Coincident(g36,g29)
    c: Horizontal(g36)
    c: Coincident(g37,g29)
    c: Coincident(g37,g30)
    c: Horizontal(g37)
    c: Coincident(g38,g30)
    c: Coincident(g38,g31)
    c: Horizontal(g38)
    c: Coincident(g39,g31)
    c: Coincident(g39,g32)
    c: Horizontal(g39)
    c: Coincident(g40,g32)
    c: Coincident(g40,g33)
    c: Horizontal(g40)
    c: Equal(g34,g35)
    c: Equal(g35,g36)
    c: Equal(g36,g37)
    c: Equal(g37,g38)
    c: Equal(g38,g39)
    c: Equal(g39,g40)
    c: Vertical(g26,g10)
    c: PointOnObject(g26,g9)
    c: Vertical(g33,g17)
    c: Equal(g27,g29)
    c: Equal(g29,g30)
    c: Equal(g30,g31)
    c: Equal(g31,g32)
    c: Equal(g32,g33)
    c: Equal(g28,g27)
    c: Equal(g11,g27)
    c: Vertical(g41)
    c: PointOnObject(g42,g-1)
    c: Vertical(g42)
    c: DistanceY(g41,g41) = 304.8
    c: PointOnObject(g41,g-1)
    c: Symmetric(g42,g41,g-2)
    c: DistanceX(g41,g42) = 1035.05
    c: DistanceX(g41,g9) = 69.85
    c: PointOnObject(g2,g7)
    c: Coincident(g0,g7)
    c: PointOnObject(g4,g1)
    c: Equal(g0,g4)
    c: DistanceX(g5,g5) = 889
    c: Vertical(g0,g1)
    c: PointOnObject(g9,g0)
    c: Coincident(g1,g6)
    c: DistanceY(g0,g0) = 50.8
FEATURE [Sketcher::SketchObject] Sketch006  label="magnet-backersk"
  ArcFitTolerance = 1e-06
  ExternalTypes = [0]
  FullyConstrained = true
  MakeInternals = false
  MapMode = 5
  Placement = pos=(0,-307.975,0) rot=(1,0,0;1.5708rad)
  expr: Constraints[8] = 12 in
  sketch-geometry (10):
    g0: LineSegment StartX=-447.675 StartY=50.8 StartZ=0 EndX=441.325 EndY=50.8 EndZ=0
    g1: LineSegment StartX=441.325 StartY=0 StartZ=0 EndX=-447.675 EndY=0 EndZ=0
    g2: LineSegment [constr] StartX=-517.525 StartY=304.8 StartZ=0 EndX=-517.525 EndY=0 EndZ=0
    g3: LineSegment [constr] StartX=517.525 StartY=304.8 StartZ=0 EndX=517.525 EndY=0 EndZ=0
    g4: LineSegment StartX=-447.675 StartY=50.8 StartZ=0 EndX=-447.675 EndY=0 EndZ=0
    g5: LineSegment StartX=441.325 StartY=50.8 StartZ=0 EndX=441.325 EndY=0 EndZ=0
    g6: LineSegment StartX=-447.675 StartY=133.35 StartZ=0 EndX=-447.675 EndY=82.55 EndZ=0
    g7: LineSegment StartX=-447.675 StartY=82.55 StartZ=0 EndX=441.325 EndY=82.55 EndZ=0
    g8: LineSegment StartX=441.325 StartY=82.55 StartZ=0 EndX=441.325 EndY=133.35 EndZ=0
    g9: LineSegment StartX=441.325 StartY=133.35 StartZ=0 EndX=-447.675 EndY=133.35 EndZ=0
  constraints (32):
    c: Horizontal(g0)
    c: Horizontal(g1)
    c: DistanceY(g1,g0) = 50.8
    c: Vertical(g2)
    c: PointOnObject(g2,g-1)
    c: PointOnObject(g3,g-1)
    c: Vertical(g3)
    c: Symmetric(g3,g2,g-2)
    c: DistanceY(g2,g2) = 304.8
    c: DistanceY(g2,g2) = 304.8
    c: DistanceX(g2,g3) = 1035.05
    c: Coincident(g4,g0)
    c: Coincident(g4,g1)
    c: Vertical(g4)
    c: Coincident(g5,g0)
    c: Coincident(g5,g1)
    c: Vertical(g5)
    c: DistanceX(g0,g0) = 889
    c: DistanceX(g2,g1) = 69.85
    c: PointOnObject(g1,g-1)
    c: Coincident(g6,g7)
    c: Coincident(g7,g8)
    c: Coincident(g8,g9)
    c: Coincident(g9,g6)
    c: Vertical(g6)
    c: Vertical(g8)
    c: Horizontal(g7)
    c: Horizontal(g9)
    c: PointOnObject(g7,g5)
    c: PointOnObject(g6,g4)
    c: DistanceY(g0,g6) = 31.75
    c: Equal(g6,g4)
FEATURE [Sketcher::SketchObject] Sketch007
  ArcFitTolerance = 1e-06
  ExternalTypes = [0]
  FullyConstrained = true
  MakeInternals = false
  MapMode = 5
  Placement = pos=(-520.7,0,0) rot=(0.57735,0.57735,0.57735;2.0944rad)
  sketch-geometry (4):
    g0: LineSegment StartX=-314.325 StartY=304.8 StartZ=0 EndX=-314.325 EndY=0 EndZ=0
    g1: LineSegment StartX=-314.325 StartY=0 StartZ=0 EndX=314.325 EndY=0 EndZ=0
    g2: LineSegment StartX=314.325 StartY=0 StartZ=0 EndX=314.325 EndY=304.8 EndZ=0
    g3: LineSegment StartX=314.325 StartY=304.8 StartZ=0 EndX=-314.325 EndY=304.8 EndZ=0
  constraints (11):
    c: Coincident(g0,g1)
    c: Coincident(g1,g2)
    c: Coincident(g2,g3)
    c: Coincident(g3,g0)
    c: Vertical(g0)
    c: Vertical(g2)
    c: Horizontal(g1)
    c: PointOnObject(g1,g-1)
    c: DistanceY(g2,g2) = 304.8
    c: DistanceX(g3,g3) = 628.65
    c: Symmetric(g0,g2,g-2)
FEATURE [PartDesign::Body] Body004  label="back"
  AllowCompound = false
  Origin = -> Origin010
FEATURE [Sketcher::SketchObject] Sketch008
  ArcFitTolerance = 1e-06
  ExternalTypes = [0]
  FullyConstrained = true
  MakeInternals = false
  MapMode = 5
  Placement = pos=(520.7,0,0) rot=(0.57735,0.57735,0.57735;2.0944rad)
  sketch-geometry (8):
    g0: LineSegment StartX=-314.325 StartY=304.8 StartZ=0 EndX=-314.325 EndY=0 EndZ=0
    g1: LineSegment StartX=-314.325 StartY=0 StartZ=0 EndX=314.325 EndY=0 EndZ=0
    g2: LineSegment StartX=314.325 StartY=0 StartZ=0 EndX=314.325 EndY=304.8 EndZ=0
    g3: LineSegment StartX=314.325 StartY=304.8 StartZ=0 EndX=-314.325 EndY=304.8 EndZ=0
    g4: LineSegment StartX=-279.4 StartY=285.75 StartZ=0 EndX=-279.4 EndY=31.75 EndZ=0
    g5: LineSegment StartX=-279.4 StartY=31.75 StartZ=0 EndX=279.4 EndY=31.75 EndZ=0
    g6: LineSegment StartX=279.4 StartY=31.75 StartZ=0 EndX=279.4 EndY=285.75 EndZ=0
    g7: LineSegment StartX=279.4 StartY=285.75 StartZ=0 EndX=-279.4 EndY=285.75 EndZ=0
  constraints (22):
    c: Coincident(g0,g1)
    c: Coincident(g1,g2)
    c: Coincident(g2,g3)
    c: Coincident(g3,g0)
    c: Vertical(g0)
    c: Vertical(g2)
    c: Horizontal(g1)
    c: PointOnObject(g1,g-1)
    c: DistanceX(g3,g3) = 628.65
    c: Symmetric(g0,g2,g-2)
    c: DistanceY(g0,g0) = 304.8
    c: Coincident(g4,g5)
    c: Coincident(g5,g6)
    c: Coincident(g6,g7)
    c: Coincident(g7,g4)
    c: Vertical(g4)
    c: Vertical(g6)
    c: Horizontal(g7)
    c: Symmetric(g5,g4,g-2)
    c: DistanceX(g5,g5) = 558.8
    c: DistanceY(g6,g6) = 254
    c: DistanceY(g-1,g5) = 31.75
FEATURE [PartDesign::Pad] Pad006
  Direction = (1,0,0)
  Length = 2.54
  Length2 = 10
  Placement = pos=(520.7,0,0) rot=(0.57735,0.57735,0.57735;2.0944rad)
  Profile = -> Sketch008
  ReferenceAxis = -> Sketch008 [N_Axis]
  Reversed = true
  Suppressed = false
  Type = 0
FEATURE [PartDesign::Body] Body006  label="right"
  AllowCompound = false
  Group = -> [Sketch008,Pad006]
  Origin = -> Origin014
  Tip = -> Pad006
FEATURE [PartDesign::Pad] Pad007
  Direction = (1,0,0)
  Length = 3.175
  Length2 = 10
  Placement = pos=(-520.7,0,0) rot=(0.57735,0.57735,0.57735;2.0944rad)
  Profile = -> Sketch007
  ReferenceAxis = -> Sketch007 [N_Axis]
  Suppressed = false
  Type = 0
FEATURE [PartDesign::Body] Body005  label="left"
  AllowCompound = false
  Group = -> [Sketch007,Pad007]
  Origin = -> Origin012
  Tip = -> Pad007
FEATURE [PartDesign::Pad] Pad008
  BaseFeature = -> Pad002
  Direction = (0,-1,-2e-16)
  Length = 3.175
  Length2 = 10
  Placement = pos=(0,-311.15,0) rot=(1,0,0;1.5708rad)
  Profile = -> Sketch005
  ReferenceAxis = -> Sketch005 [N_Axis]
  Reversed = true
  Suppressed = false
  Type = 0
FEATURE [PartDesign::Pad] Pad009
  BaseFeature = -> Pad008
  Direction = (0,-1,-2e-16)
  Length = 3.175
  Length2 = 10
  Placement = pos=(0,-311.15,0) rot=(1,0,0;1.5708rad)
  Profile = -> Sketch006
  ReferenceAxis = -> Sketch006 [N_Axis]
  Reversed = true
  Suppressed = false
  Type = 0
FEATURE [PartDesign::Body] Body003  label="front"
  AllowCompound = false
  Group = -> [Sketch004,Pad002,Sketch005,Sketch006,Pad008,Pad009]
  Origin = -> Origin008
  Tip = -> Pad009
FEATURE [App::Part] Part  label="enclosure"
  Group = -> [Body,Body003,Body004,Body005,Body006]
  Origin = -> Origin004
FEATURE [App::Point] Origin015  label="Origin"
  Role = Origin
FEATURE [App::Point] Origin017  label="Origin"
  Role = Origin
FEATURE [App::Point] Origin018  label="Origin"
  Role = Origin
FEATURE [App::Point] Origin019  label="Origin"
  Role = Origin
FEATURE [App::Point] Origin020  label="Origin"
  Role = Origin
FEATURE [App::Point] Origin021  label="Origin"
  Role = Origin
COMPONENT P7 — recipe-attached ("lid", a linked part whose construction recipe lives in a companion FreeCAD document of the same project; that document's serialized recipe follows).
Construction recipe (the companion document, serialized — sketch geometry with constraints, then the solid features built on it; lengths are millimeters unless a unit is written):

FCSTD DOCUMENT  (FreeCAD 1.1R40971 (Git))
Label: lid
License: All rights reserved
LicenseURL: http://en.wikipedia.org/wiki/All_rights_reserved
objects: Sketcher::SketchObject×4, App::Point×3, PartDesign::Pad×3, PartDesign::Body×2, PartDesign::Thickness×1, PartDesign::Pocket×1, App::Part×1
note: 25 computed .brp shape members not serialized (recipe doc carries the construction recipe); baked Part::Feature solids carry a one-line shape summary decoded from their .brp

FEATURE [App::Point] Origin001
  Role = Origin
FEATURE [Sketcher::SketchObject] Sketch
  ArcFitTolerance = 1e-06
  AttachmentSupport = -> [XY_Plane]
  ExternalTypes = [0]
  FullyConstrained = true
  MakeInternals = false
  MapMode = 5
  sketch-geometry (8):
    g0: LineSegment StartX=-527.05 StartY=323.85 StartZ=0 EndX=-527.05 EndY=-323.85 EndZ=0
    g1: LineSegment StartX=-527.05 StartY=-323.85 StartZ=0 EndX=527.05 EndY=-323.85 EndZ=0
    g2: LineSegment StartX=527.05 StartY=-323.85 StartZ=0 EndX=527.05 EndY=323.85 EndZ=0
    g3: LineSegment StartX=527.05 StartY=323.85 StartZ=0 EndX=-527.05 EndY=323.85 EndZ=0
    g4: LineSegment [constr] StartX=-412.75 StartY=304.8 StartZ=0 EndX=-412.75 EndY=-304.8 EndZ=0
    g5: LineSegment [constr] StartX=-412.75 StartY=-304.8 StartZ=0 EndX=501.65 EndY=-304.8 EndZ=0
    g6: LineSegment [constr] StartX=501.65 StartY=-304.8 StartZ=0 EndX=501.65 EndY=304.8 EndZ=0
    g7: LineSegment [constr] StartX=501.65 StartY=304.8 StartZ=0 EndX=-412.75 EndY=304.8 EndZ=0
  constraints (22):
    c: Coincident(g0,g1)
    c: Coincident(g1,g2)
    c: Coincident(g2,g3)
    c: Coincident(g3,g0)
    c: Vertical(g2)
    c: Horizontal(g1)
    c: Coincident(g4,g5)
    c: Coincident(g5,g6)
    c: Coincident(g6,g7)
    c: Coincident(g7,g4)
    c: Vertical(g6)
    c: Horizontal(g5)
    c: Horizontal(g7)
    c: DistanceY(g6,g6) = 609.6
    c: DistanceX(g7,g7) = 914.4
    c: DistanceX(g3,g3) = 1054.1
    c: DistanceY(g2,g2) = 647.7
    c: Symmetric(g0,g2,g-2)
    c: Symmetric(g0,g0,g-1)
    c: DistanceX(g6,g2) = 25.4
    c: DistanceX(g0,g4) = 114.3
    c: Symmetric(g4,g4,g-1)
FEATURE [PartDesign::Pad] Pad
  Direction = (0,0,1)
  Length = 50.8
  Length2 = 10
  Profile = -> Sketch
  ReferenceAxis = -> Sketch [N_Axis]
  Reversed = true
  Suppressed = false
  Type = 0
FEATURE [App::Point] Origin003
  Role = Origin
FEATURE [Sketcher::SketchObject] Sketch001
  ArcFitTolerance = 1e-06
  AttachmentSupport = -> [XY_Plane001]
  ExternalTypes = [0]
  FullyConstrained = true
  MakeInternals = false
  MapMode = 5
  sketch-geometry (4):
    g0: LineSegment StartX=-412.75 StartY=304.8 StartZ=0 EndX=-412.75 EndY=-304.8 EndZ=0
    g1: LineSegment StartX=-412.75 StartY=-304.8 StartZ=0 EndX=501.65 EndY=-304.8 EndZ=0
    g2: LineSegment StartX=501.65 StartY=-304.8 StartZ=0 EndX=501.65 EndY=304.8 EndZ=0
    g3: LineSegment StartX=501.65 StartY=304.8 StartZ=0 EndX=-412.75 EndY=304.8 EndZ=0
  constraints (11):
    c: Coincident(g0,g1)
    c: Coincident(g1,g2)
    c: Coincident(g2,g3)
    c: Coincident(g3,g0)
    c: Vertical(g0)
    c: Horizontal(g1)
    c: Horizontal(g3)
    c: DistanceY(g2,g2) = 609.6
    c: DistanceX(g3,g3) = 914.4
    c: Symmetric(g2,g1,g-1)
    c: DistanceX(g-1,g2) = 501.65
FEATURE [PartDesign::Pad] Pad001
  Direction = (0,0,1)
  Length = 6.35
  Length2 = 10
  Profile = -> Sketch001
  ReferenceAxis = -> Sketch001 [N_Axis]
  Reversed = true
  Suppressed = false
  Type = 0
FEATURE [PartDesign::Body] Body001  label="window"
  AllowCompound = false
  Group = -> [Sketch001,Pad001]
  Origin = -> Origin002
  Tip = -> Pad001
FEATURE [PartDesign::Thickness] Thickness
  Base = -> Pad [Face6]
  BaseFeature = -> Pad
  Intersection = false
  Join = 0
  Mode = 0
  Reversed = true
  SupportTransform = false
  Suppressed = false
  Value = 3.302
FEATURE [Sketcher::SketchObject] Sketch005  label="windowsk"
  ArcFitTolerance = 1e-06
  AttachmentSupport = -> [XY_Plane]
  ExternalGeometry = -> [Thickness]
  ExternalTypes = [0]
  FullyConstrained = true
  MakeInternals = false
  MapMode = 5
  sketch-geometry (4):
    g0: LineSegment StartX=-412.75 StartY=304.8 StartZ=0 EndX=-412.75 EndY=-304.8 EndZ=0
    g1: LineSegment StartX=-412.75 StartY=-304.8 StartZ=0 EndX=501.65 EndY=-304.8 EndZ=0
    g2: LineSegment StartX=501.65 StartY=-304.8 StartZ=0 EndX=501.65 EndY=304.8 EndZ=0
    g3: LineSegment StartX=501.65 StartY=304.8 StartZ=0 EndX=-412.75 EndY=304.8 EndZ=0
  constraints (12):
    c: Coincident(g0,g1)
    c: Coincident(g1,g2)
    c: Coincident(g2,g3)
    c: Coincident(g3,g0)
    c: Vertical(g2)
    c: Horizontal(g1)
    c: Horizontal(g3)
    c: DistanceX(g3,g3) = 914.4
    c: DistanceY(g0,g0) = 609.6
    c: DistanceX(g-1,g1) = 501.65
    c: DistanceX(g-3,g0) = 114.3
    c: Symmetric(g0,g0,g-1)
FEATURE [App::Point] Origin007
  Role = Origin
FEATURE [Sketcher::SketchObject] Sketch006  label="ribsk"
  ArcFitTolerance = 1e-06
  AttachmentSupport = -> [XY_Plane]
  ExternalTypes = [0]
  FullyConstrained = true
  MakeInternals = false
  MapMode = 5
  sketch-geometry (28):
    g0: LineSegment StartX=-527.05 StartY=1.651 StartZ=0 EndX=-527.05 EndY=-1.651 EndZ=0
    g1: LineSegment StartX=-527.05 StartY=-1.651 StartZ=0 EndX=-419.354 EndY=-1.651 EndZ=0
    g2: LineSegment StartX=527.05 StartY=-1.651 StartZ=0 EndX=527.05 EndY=1.651 EndZ=0
    g3: LineSegment StartX=527.05 StartY=1.651 StartZ=0 EndX=200.152 EndY=1.651 EndZ=0
    g4: LineSegment StartX=-111.252 StartY=323.85 StartZ=0 EndX=-111.252 EndY=1.651 EndZ=0
    g5: LineSegment StartX=-111.252 StartY=-323.85 StartZ=0 EndX=-107.95 EndY=-323.85 EndZ=0
    g6: LineSegment StartX=-107.95 StartY=-323.85 StartZ=0 EndX=-107.95 EndY=-1.651 EndZ=0
    g7: LineSegment StartX=-107.95 StartY=323.85 StartZ=0 EndX=-111.252 EndY=323.85 EndZ=0
    g8: LineSegment StartX=200.152 StartY=323.85 StartZ=0 EndX=200.152 EndY=1.651 EndZ=0
    g9: LineSegment StartX=200.152 StartY=-323.85 StartZ=0 EndX=196.85 EndY=-323.85 EndZ=0
    g10: LineSegment StartX=196.85 StartY=-323.85 StartZ=0 EndX=196.85 EndY=-1.651 EndZ=0
    g11: LineSegment StartX=196.85 StartY=323.85 StartZ=0 EndX=200.152 EndY=323.85 EndZ=0
    g12: LineSegment StartX=-111.252 StartY=1.651 StartZ=0 EndX=-416.052 EndY=1.651 EndZ=0
    g13: LineSegment StartX=-107.95 StartY=1.651 StartZ=0 EndX=-107.95 EndY=323.85 EndZ=0
    g14: LineSegment StartX=-111.252 StartY=-1.651 StartZ=0 EndX=-111.252 EndY=-323.85 EndZ=0
    g15: LineSegment StartX=-107.95 StartY=-1.651 StartZ=0 EndX=196.85 EndY=-1.651 EndZ=0
    g16: LineSegment StartX=200.152 StartY=-1.651 StartZ=0 EndX=527.05 EndY=-1.651 EndZ=0
    g17: LineSegment StartX=200.152 StartY=-1.651 StartZ=0 EndX=200.152 EndY=-323.85 EndZ=0
    g18: LineSegment StartX=196.85 StartY=1.651 StartZ=0 EndX=196.85 EndY=323.85 EndZ=0
    g19: LineSegment StartX=-419.354 StartY=323.85 StartZ=0 EndX=-419.354 EndY=1.651 EndZ=0
    g20: LineSegment StartX=-419.354 StartY=-323.85 StartZ=0 EndX=-416.052 EndY=-323.85 EndZ=0
    g21: LineSegment StartX=-416.052 StartY=-323.85 StartZ=0 EndX=-416.052 EndY=-1.651 EndZ=0
    g22: LineSegment StartX=-416.052 StartY=323.85 StartZ=0 EndX=-419.354 EndY=323.85 EndZ=0
    g23: LineSegment StartX=-419.354 StartY=1.651 StartZ=0 EndX=-527.05 EndY=1.651 EndZ=0
    g24: LineSegment StartX=-416.052 StartY=1.651 StartZ=0 EndX=-416.052 EndY=323.85 EndZ=0
    g25: LineSegment StartX=-416.052 StartY=-1.651 StartZ=0 EndX=-111.252 EndY=-1.651 EndZ=0
    g26: LineSegment StartX=-419.354 StartY=-1.651 StartZ=0 EndX=-419.354 EndY=-323.85 EndZ=0
    g27: LineSegment StartX=-107.95 StartY=1.651 StartZ=0 EndX=196.85 EndY=1.651 EndZ=0
  constraints (80):
    c: Coincident(g0,g1)
    c: Coincident(g16,g2)
    c: Coincident(g2,g3)
    c: Coincident(g23,g0)
    c: Vertical(g2)
    c: Coincident(g14,g5)
    c: Coincident(g5,g6)
    c: Coincident(g13,g7)
    c: Coincident(g7,g4)
    c: Horizontal(g5)
    c: Horizontal(g7)
    c: Coincident(g17,g9)
    c: Coincident(g9,g10)
    c: Coincident(g18,g11)
    c: Coincident(g11,g8)
    c: Horizontal(g9)
    c: Horizontal(g11)
    c: Vertical(g6)
    c: Vertical(g13)
    c: Vertical(g4)
    c: Vertical(g14)
    c: Coincident(g12,g4)
    c: Coincident(g6,g15)
    c: Coincident(g14,g25)
    c: Vertical(g8)
    c: Vertical(g17)
    c: Vertical(g10)
    c: Vertical(g18)
    c: Equal(g5,g9)
    c: Equal(g9,g2)
    c: PointOnObject(g13,g6)
    c: Symmetric(g0,g0,g-1)
    c: Symmetric(g5,g4,g-1)
    c: Symmetric(g9,g8,g-1)
    c: Horizontal(g5,g9)
    c: DistanceY(g9,g8) = 647.7
    c: DistanceX(g0,g2) = 1054.1
    c: Symmetric(g0,g2,g-2)
    c: Distance(g11,g-2) = 196.85
    c: Coincident(g26,g20)
    c: Coincident(g20,g21)
    c: Coincident(g24,g22)
    c: Coincident(g22,g19)
    c: Horizontal(g20)
    c: Horizontal(g22)
    c: Equal(g2,g20)
    c: Horizontal(g12)
    c: Horizontal(g23)
    c: Horizontal(g7,g24)
    c: Horizontal(g5,g20)
    c: PointOnObject(g23,g12)
    c: DistanceX(g12,g12) = 304.8
    c: Vertical(g21)
    c: Vertical(g24)
    c: Coincident(g12,g24)
    c: Horizontal(g1)
    c: Horizontal(g25)
    c: PointOnObject(g6,g1)
    c: Coincident(g21,g25)
    c: Vertical(g19)
    c: Vertical(g26)
    c: Coincident(g23,g19)
    c: Coincident(g1,g26)
    c: PointOnObject(g1,g19)
    c: PointOnObject(g21,g24)
    c: PointOnObject(g21,g1)
    c: DistanceX(g22,g22) = 3.302
    c: Horizontal(g3)
    c: Coincident(g8,g3)
    c: PointOnObject(g4,g3)
    c: Coincident(g27,g13)
    c: Coincident(g27,g18)
    c: Horizontal(g27)
    c: PointOnObject(g13,g12)
    c: Equal(g12,g27)
    c: Horizontal(g15)
    c: Coincident(g15,g10)
    c: Horizontal(g16)
    c: Coincident(g16,g17)
    c: PointOnObject(g10,g18)
FEATURE [PartDesign::Pad] Pad002
  BaseFeature = -> Thickness
  Direction = (0,0,1)
  Length = 31.75
  Length2 = 10
  Profile = -> Sketch006
  ReferenceAxis = -> Sketch006 [N_Axis]
  Reversed = true
  Suppressed = false
  Type = 0
FEATURE [PartDesign::Pocket] Pocket
  BaseFeature = -> Pad002
  Direction = (0,0,-1)
  Length = 6.35
  Length2 = 5
  Profile = -> Sketch005
  ReferenceAxis = -> Sketch005 [N_Axis]
  Suppressed = false
  Type = 0
FEATURE [PartDesign::Body] Body  label="top"
  AllowCompound = false
  Group = -> [Sketch,Pad,Thickness,Sketch005,Sketch006,Pad002,Pocket]
  Origin = -> Origin
  Tip = -> Pocket
FEATURE [App::Part] Part  label="lid"
  Group = -> [Body,Body001]
  Origin = -> Origin006
PROVENANCE & LICENSES
A FreeCAD (.FCStd) document from a public repository crawl; recipes are the document's own serialized feature recipes (and, for linked parts, companion documents' recipes).
License: as declared in the source repository (recorded in the dataset sidecar).
